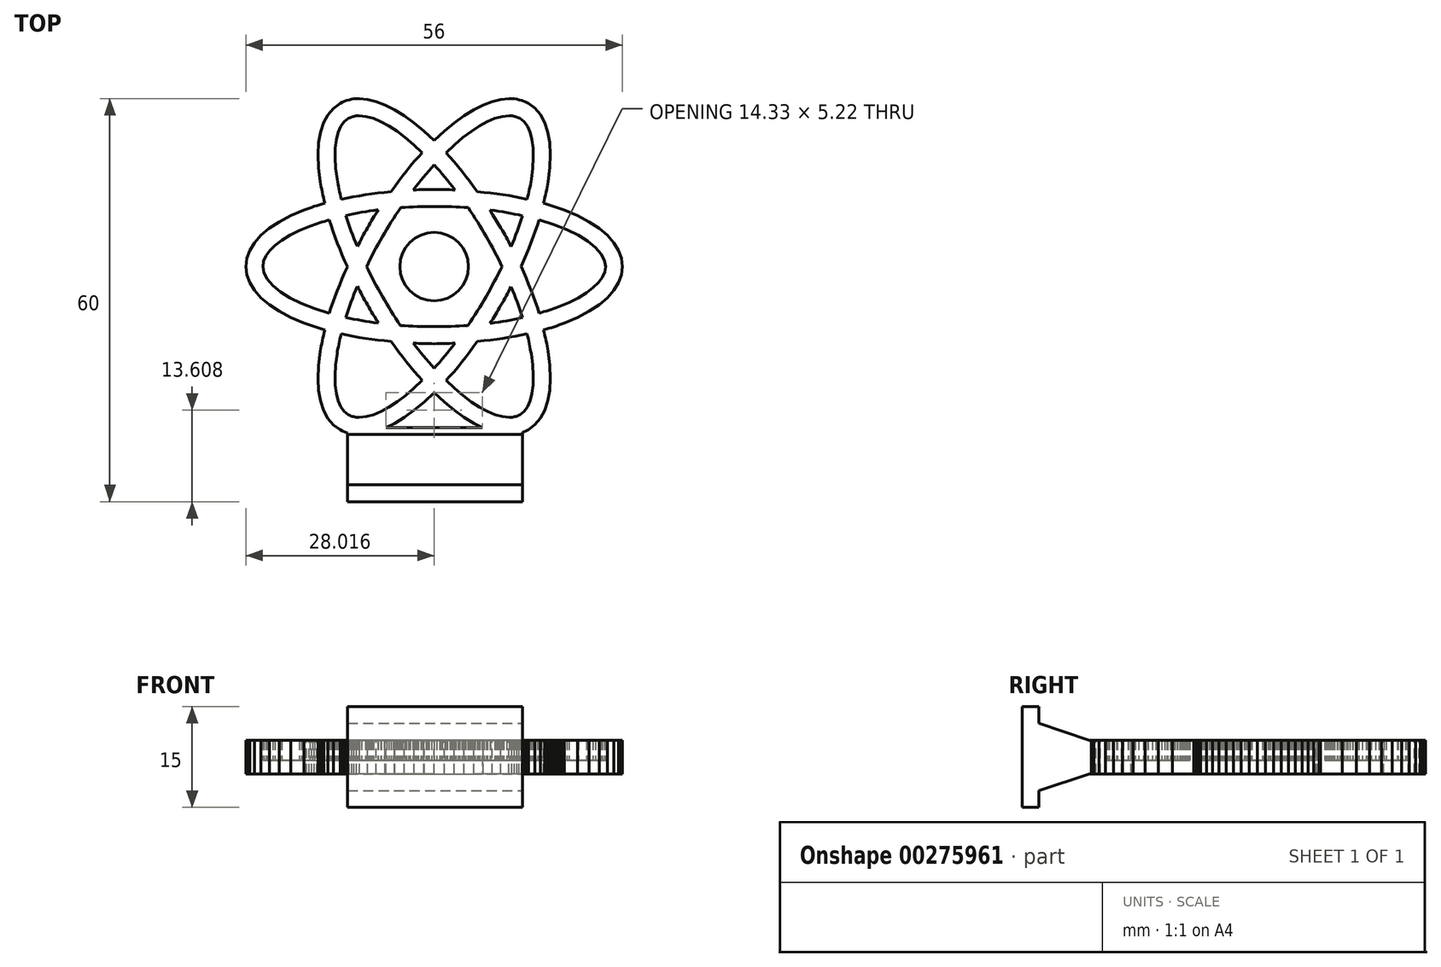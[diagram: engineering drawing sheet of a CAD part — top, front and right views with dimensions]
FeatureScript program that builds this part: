
annotation { "Feature Type Name" : "Feature", "Feature Type Description" : "" }
export const myFeature = defineFeature(function(context is Context, id is Id, definition is map)
    precondition{}
    {
        {
            var Q0;
            Q0=qCreatedBy(makeId("Top.planeOp"),FACE);
            var sketch = newSketch(context, id + "F0", { "sketchPlane" : qUnion([Q0])});
            skLineSegment(sketch, "E0", {"start": v(0, 5.1) * mm, "end": v(1.03, 5) * mm});
            skLineSegment(sketch, "E1", {"start": v(1.03, 5) * mm, "end": v(1.98, 4.7) * mm});
            skLineSegment(sketch, "E2", {"start": v(1.98, 4.7) * mm, "end": v(2.85, 4.23) * mm});
            skLineSegment(sketch, "E3", {"start": v(2.85, 4.23) * mm, "end": v(3.6, 3.6) * mm});
            skLineSegment(sketch, "E4", {"start": v(3.6, 3.6) * mm, "end": v(4.23, 2.85) * mm});
            skLineSegment(sketch, "E5", {"start": v(4.23, 2.85) * mm, "end": v(4.7, 1.98) * mm});
            skLineSegment(sketch, "E6", {"start": v(4.7, 1.98) * mm, "end": v(5, 1.03) * mm});
            skLineSegment(sketch, "E7", {"start": v(5, 1.03) * mm, "end": v(5.1, 0) * mm});
            skLineSegment(sketch, "E8", {"start": v(5.1, 0) * mm, "end": v(5, -1.03) * mm});
            skLineSegment(sketch, "E9", {"start": v(5, -1.03) * mm, "end": v(4.7, -1.98) * mm});
            skLineSegment(sketch, "E10", {"start": v(4.7, -1.98) * mm, "end": v(4.23, -2.85) * mm});
            skLineSegment(sketch, "E11", {"start": v(4.23, -2.85) * mm, "end": v(3.6, -3.6) * mm});
            skLineSegment(sketch, "E12", {"start": v(3.6, -3.6) * mm, "end": v(2.85, -4.23) * mm});
            skLineSegment(sketch, "E13", {"start": v(2.85, -4.23) * mm, "end": v(1.98, -4.7) * mm});
            skLineSegment(sketch, "E14", {"start": v(1.98, -4.7) * mm, "end": v(1.03, -5) * mm});
            skLineSegment(sketch, "E15", {"start": v(1.03, -5) * mm, "end": v(0, -5.1) * mm});
            skLineSegment(sketch, "E16", {"start": v(0, -5.1) * mm, "end": v(-1.03, -5) * mm});
            skLineSegment(sketch, "E17", {"start": v(-1.03, -5) * mm, "end": v(-1.98, -4.7) * mm});
            skLineSegment(sketch, "E18", {"start": v(-1.98, -4.7) * mm, "end": v(-2.85, -4.23) * mm});
            skLineSegment(sketch, "E19", {"start": v(-2.85, -4.23) * mm, "end": v(-3.6, -3.6) * mm});
            skLineSegment(sketch, "E20", {"start": v(-3.6, -3.6) * mm, "end": v(-4.23, -2.85) * mm});
            skLineSegment(sketch, "E21", {"start": v(-4.23, -2.85) * mm, "end": v(-4.7, -1.98) * mm});
            skLineSegment(sketch, "E22", {"start": v(-4.7, -1.98) * mm, "end": v(-5, -1.03) * mm});
            skLineSegment(sketch, "E23", {"start": v(-5, -1.03) * mm, "end": v(-5.1, 0) * mm});
            skLineSegment(sketch, "E24", {"start": v(-5.1, 0) * mm, "end": v(-5, 1.03) * mm});
            skLineSegment(sketch, "E25", {"start": v(-5, 1.03) * mm, "end": v(-4.7, 1.98) * mm});
            skLineSegment(sketch, "E26", {"start": v(-4.7, 1.98) * mm, "end": v(-4.23, 2.85) * mm});
            skLineSegment(sketch, "E27", {"start": v(-4.23, 2.85) * mm, "end": v(-3.6, 3.6) * mm});
            skLineSegment(sketch, "E28", {"start": v(-3.6, 3.6) * mm, "end": v(-2.85, 4.23) * mm});
            skLineSegment(sketch, "E29", {"start": v(-2.85, 4.23) * mm, "end": v(-1.98, 4.7) * mm});
            skLineSegment(sketch, "E30", {"start": v(-1.98, 4.7) * mm, "end": v(-1.03, 5) * mm});
            skLineSegment(sketch, "E31", {"start": v(-1.03, 5) * mm, "end": v(0, 5.1) * mm});
            skLineSegment(sketch, "E32", {"start": v(19.36, 8.4) * mm, "end": v(19, 8.54) * mm});
            skLineSegment(sketch, "E33", {"start": v(19, 8.54) * mm, "end": v(18.62, 8.68) * mm});
            skLineSegment(sketch, "E34", {"start": v(18.62, 8.68) * mm, "end": v(18.24, 8.8) * mm});
            skLineSegment(sketch, "E35", {"start": v(18.24, 8.8) * mm, "end": v(17.86, 8.94) * mm});
            skLineSegment(sketch, "E36", {"start": v(17.86, 8.94) * mm, "end": v(17.47, 9.07) * mm});
            skLineSegment(sketch, "E37", {"start": v(17.47, 9.07) * mm, "end": v(17.08, 9.2) * mm});
            skLineSegment(sketch, "E38", {"start": v(17.08, 9.2) * mm, "end": v(16.68, 9.32) * mm});
            skLineSegment(sketch, "E39", {"start": v(16.68, 9.32) * mm, "end": v(16.28, 9.44) * mm});
            skLineSegment(sketch, "E40", {"start": v(16.28, 9.44) * mm, "end": v(16.38, 9.84) * mm});
            skLineSegment(sketch, "E41", {"start": v(16.38, 9.84) * mm, "end": v(16.47, 10.24) * mm});
            skLineSegment(sketch, "E42", {"start": v(16.47, 10.24) * mm, "end": v(16.56, 10.64) * mm});
            skLineSegment(sketch, "E43", {"start": v(16.56, 10.64) * mm, "end": v(16.65, 11.04) * mm});
            skLineSegment(sketch, "E44", {"start": v(16.65, 11.04) * mm, "end": v(16.73, 11.44) * mm});
            skLineSegment(sketch, "E45", {"start": v(16.73, 11.44) * mm, "end": v(16.8, 11.83) * mm});
            skLineSegment(sketch, "E46", {"start": v(16.8, 11.83) * mm, "end": v(16.88, 12.22) * mm});
            skLineSegment(sketch, "E47", {"start": v(16.88, 12.22) * mm, "end": v(16.95, 12.61) * mm});
            skLineSegment(sketch, "E48", {"start": v(16.95, 12.61) * mm, "end": v(17.21, 14.74) * mm});
            skLineSegment(sketch, "E49", {"start": v(17.21, 14.74) * mm, "end": v(17.29, 16.7) * mm});
            skLineSegment(sketch, "E50", {"start": v(17.29, 16.7) * mm, "end": v(17.18, 18.47) * mm});
            skLineSegment(sketch, "E51", {"start": v(17.18, 18.47) * mm, "end": v(16.9, 20.06) * mm});
            skLineSegment(sketch, "E52", {"start": v(16.9, 20.06) * mm, "end": v(16.44, 21.44) * mm});
            skLineSegment(sketch, "E53", {"start": v(16.44, 21.44) * mm, "end": v(15.8, 22.61) * mm});
            skLineSegment(sketch, "E54", {"start": v(15.8, 22.61) * mm, "end": v(14.99, 23.56) * mm});
            skLineSegment(sketch, "E55", {"start": v(14.99, 23.56) * mm, "end": v(14, 24.28) * mm});
            skLineSegment(sketch, "E56", {"start": v(14, 24.28) * mm, "end": v(13.68, 24.46) * mm});
            skLineSegment(sketch, "E57", {"start": v(13.68, 24.46) * mm, "end": v(13.34, 24.6) * mm});
            skLineSegment(sketch, "E58", {"start": v(13.34, 24.6) * mm, "end": v(13, 24.73) * mm});
            skLineSegment(sketch, "E59", {"start": v(13, 24.73) * mm, "end": v(12.65, 24.83) * mm});
            skLineSegment(sketch, "E60", {"start": v(12.65, 24.83) * mm, "end": v(12.29, 24.9) * mm});
            skLineSegment(sketch, "E61", {"start": v(12.29, 24.9) * mm, "end": v(11.92, 24.96) * mm});
            skLineSegment(sketch, "E62", {"start": v(11.92, 24.96) * mm, "end": v(11.53, 24.99) * mm});
            skLineSegment(sketch, "E63", {"start": v(11.53, 24.99) * mm, "end": v(11.14, 25) * mm});
            skLineSegment(sketch, "E64", {"start": v(11.14, 25) * mm, "end": v(9.92, 24.9) * mm});
            skLineSegment(sketch, "E65", {"start": v(9.92, 24.9) * mm, "end": v(8.64, 24.58) * mm});
            skLineSegment(sketch, "E66", {"start": v(8.64, 24.58) * mm, "end": v(7.3, 24.06) * mm});
            skLineSegment(sketch, "E67", {"start": v(7.3, 24.06) * mm, "end": v(5.9, 23.35) * mm});
            skLineSegment(sketch, "E68", {"start": v(5.9, 23.35) * mm, "end": v(4.47, 22.46) * mm});
            skLineSegment(sketch, "E69", {"start": v(4.47, 22.46) * mm, "end": v(3, 21.4) * mm});
            skLineSegment(sketch, "E70", {"start": v(3, 21.4) * mm, "end": v(1.5, 20.17) * mm});
            skLineSegment(sketch, "E71", {"start": v(1.5, 20.17) * mm, "end": v(0, 18.78) * mm});
            skLineSegment(sketch, "E72", {"start": v(0, 18.78) * mm, "end": v(-1.5, 20.17) * mm});
            skLineSegment(sketch, "E73", {"start": v(-1.5, 20.17) * mm, "end": v(-3, 21.4) * mm});
            skLineSegment(sketch, "E74", {"start": v(-3, 21.4) * mm, "end": v(-4.47, 22.46) * mm});
            skLineSegment(sketch, "E75", {"start": v(-4.47, 22.46) * mm, "end": v(-5.9, 23.35) * mm});
            skLineSegment(sketch, "E76", {"start": v(-5.9, 23.35) * mm, "end": v(-7.3, 24.06) * mm});
            skLineSegment(sketch, "E77", {"start": v(-7.3, 24.06) * mm, "end": v(-8.64, 24.58) * mm});
            skLineSegment(sketch, "E78", {"start": v(-8.64, 24.58) * mm, "end": v(-9.92, 24.9) * mm});
            skLineSegment(sketch, "E79", {"start": v(-9.92, 24.9) * mm, "end": v(-11.14, 25) * mm});
            skLineSegment(sketch, "E80", {"start": v(-11.14, 25) * mm, "end": v(-11.53, 24.99) * mm});
            skLineSegment(sketch, "E81", {"start": v(-11.53, 24.99) * mm, "end": v(-11.92, 24.96) * mm});
            skLineSegment(sketch, "E82", {"start": v(-11.92, 24.96) * mm, "end": v(-12.29, 24.9) * mm});
            skLineSegment(sketch, "E83", {"start": v(-12.29, 24.9) * mm, "end": v(-12.65, 24.83) * mm});
            skLineSegment(sketch, "E84", {"start": v(-12.65, 24.83) * mm, "end": v(-13, 24.73) * mm});
            skLineSegment(sketch, "E85", {"start": v(-13, 24.73) * mm, "end": v(-13.34, 24.6) * mm});
            skLineSegment(sketch, "E86", {"start": v(-13.34, 24.6) * mm, "end": v(-13.68, 24.46) * mm});
            skLineSegment(sketch, "E87", {"start": v(-13.68, 24.46) * mm, "end": v(-14, 24.28) * mm});
            skLineSegment(sketch, "E88", {"start": v(-14, 24.28) * mm, "end": v(-14.99, 23.55) * mm});
            skLineSegment(sketch, "E89", {"start": v(-14.99, 23.55) * mm, "end": v(-15.8, 22.59) * mm});
            skLineSegment(sketch, "E90", {"start": v(-15.8, 22.59) * mm, "end": v(-16.44, 21.4) * mm});
            skLineSegment(sketch, "E91", {"start": v(-16.44, 21.4) * mm, "end": v(-16.9, 20.02) * mm});
            skLineSegment(sketch, "E92", {"start": v(-16.9, 20.02) * mm, "end": v(-17.18, 18.44) * mm});
            skLineSegment(sketch, "E93", {"start": v(-17.18, 18.44) * mm, "end": v(-17.29, 16.67) * mm});
            skLineSegment(sketch, "E94", {"start": v(-17.29, 16.67) * mm, "end": v(-17.21, 14.73) * mm});
            skLineSegment(sketch, "E95", {"start": v(-17.21, 14.73) * mm, "end": v(-16.95, 12.61) * mm});
            skLineSegment(sketch, "E96", {"start": v(-16.95, 12.61) * mm, "end": v(-16.88, 12.22) * mm});
            skLineSegment(sketch, "E97", {"start": v(-16.88, 12.22) * mm, "end": v(-16.8, 11.83) * mm});
            skLineSegment(sketch, "E98", {"start": v(-16.8, 11.83) * mm, "end": v(-16.73, 11.44) * mm});
            skLineSegment(sketch, "E99", {"start": v(-16.73, 11.44) * mm, "end": v(-16.65, 11.04) * mm});
            skLineSegment(sketch, "E100", {"start": v(-16.65, 11.04) * mm, "end": v(-16.56, 10.64) * mm});
            skLineSegment(sketch, "E101", {"start": v(-16.56, 10.64) * mm, "end": v(-16.47, 10.24) * mm});
            skLineSegment(sketch, "E102", {"start": v(-16.47, 10.24) * mm, "end": v(-16.38, 9.84) * mm});
            skLineSegment(sketch, "E103", {"start": v(-16.38, 9.84) * mm, "end": v(-16.28, 9.44) * mm});
            skLineSegment(sketch, "E104", {"start": v(-16.28, 9.44) * mm, "end": v(-16.68, 9.32) * mm});
            skLineSegment(sketch, "E105", {"start": v(-16.68, 9.32) * mm, "end": v(-17.08, 9.2) * mm});
            skLineSegment(sketch, "E106", {"start": v(-17.08, 9.2) * mm, "end": v(-17.47, 9.08) * mm});
            skLineSegment(sketch, "E107", {"start": v(-17.47, 9.08) * mm, "end": v(-17.86, 8.96) * mm});
            skLineSegment(sketch, "E108", {"start": v(-17.86, 8.96) * mm, "end": v(-18.24, 8.83) * mm});
            skLineSegment(sketch, "E109", {"start": v(-18.24, 8.83) * mm, "end": v(-18.62, 8.7) * mm});
            skLineSegment(sketch, "E110", {"start": v(-18.62, 8.7) * mm, "end": v(-19, 8.55) * mm});
            skLineSegment(sketch, "E111", {"start": v(-19, 8.55) * mm, "end": v(-19.36, 8.4) * mm});
            skLineSegment(sketch, "E112", {"start": v(-19.36, 8.4) * mm, "end": v(-21.34, 7.57) * mm});
            skLineSegment(sketch, "E113", {"start": v(-21.34, 7.57) * mm, "end": v(-23.07, 6.65) * mm});
            skLineSegment(sketch, "E114", {"start": v(-23.07, 6.65) * mm, "end": v(-24.55, 5.68) * mm});
            skLineSegment(sketch, "E115", {"start": v(-24.55, 5.68) * mm, "end": v(-25.78, 4.64) * mm});
            skLineSegment(sketch, "E116", {"start": v(-25.78, 4.64) * mm, "end": v(-26.74, 3.55) * mm});
            skLineSegment(sketch, "E117", {"start": v(-26.74, 3.55) * mm, "end": v(-27.43, 2.4) * mm});
            skLineSegment(sketch, "E118", {"start": v(-27.43, 2.4) * mm, "end": v(-27.85, 1.22) * mm});
            skLineSegment(sketch, "E119", {"start": v(-27.85, 1.22) * mm, "end": v(-28, 0) * mm});
            skLineSegment(sketch, "E120", {"start": v(-28, 0) * mm, "end": v(-27.85, -1.22) * mm});
            skLineSegment(sketch, "E121", {"start": v(-27.85, -1.22) * mm, "end": v(-27.43, -2.4) * mm});
            skLineSegment(sketch, "E122", {"start": v(-27.43, -2.4) * mm, "end": v(-26.73, -3.55) * mm});
            skLineSegment(sketch, "E123", {"start": v(-26.73, -3.55) * mm, "end": v(-25.76, -4.64) * mm});
            skLineSegment(sketch, "E124", {"start": v(-25.76, -4.64) * mm, "end": v(-24.53, -5.68) * mm});
            skLineSegment(sketch, "E125", {"start": v(-24.53, -5.68) * mm, "end": v(-23.05, -6.65) * mm});
            skLineSegment(sketch, "E126", {"start": v(-23.05, -6.65) * mm, "end": v(-21.33, -7.57) * mm});
            skLineSegment(sketch, "E127", {"start": v(-21.33, -7.57) * mm, "end": v(-19.36, -8.4) * mm});
            skLineSegment(sketch, "E128", {"start": v(-19.36, -8.4) * mm, "end": v(-19, -8.54) * mm});
            skLineSegment(sketch, "E129", {"start": v(-19, -8.54) * mm, "end": v(-18.62, -8.68) * mm});
            skLineSegment(sketch, "E130", {"start": v(-18.62, -8.68) * mm, "end": v(-18.24, -8.8) * mm});
            skLineSegment(sketch, "E131", {"start": v(-18.24, -8.8) * mm, "end": v(-17.86, -8.94) * mm});
            skLineSegment(sketch, "E132", {"start": v(-17.86, -8.94) * mm, "end": v(-17.47, -9.07) * mm});
            skLineSegment(sketch, "E133", {"start": v(-17.47, -9.07) * mm, "end": v(-17.08, -9.2) * mm});
            skLineSegment(sketch, "E134", {"start": v(-17.08, -9.2) * mm, "end": v(-16.68, -9.32) * mm});
            skLineSegment(sketch, "E135", {"start": v(-16.68, -9.32) * mm, "end": v(-16.28, -9.44) * mm});
            skLineSegment(sketch, "E136", {"start": v(-16.28, -9.44) * mm, "end": v(-16.38, -9.84) * mm});
            skLineSegment(sketch, "E137", {"start": v(-16.38, -9.84) * mm, "end": v(-16.47, -10.24) * mm});
            skLineSegment(sketch, "E138", {"start": v(-16.47, -10.24) * mm, "end": v(-16.56, -10.64) * mm});
            skLineSegment(sketch, "E139", {"start": v(-16.56, -10.64) * mm, "end": v(-16.65, -11.04) * mm});
            skLineSegment(sketch, "E140", {"start": v(-16.65, -11.04) * mm, "end": v(-16.73, -11.44) * mm});
            skLineSegment(sketch, "E141", {"start": v(-16.73, -11.44) * mm, "end": v(-16.8, -11.83) * mm});
            skLineSegment(sketch, "E142", {"start": v(-16.8, -11.83) * mm, "end": v(-16.88, -12.22) * mm});
            skLineSegment(sketch, "E143", {"start": v(-16.88, -12.22) * mm, "end": v(-16.95, -12.61) * mm});
            skLineSegment(sketch, "E144", {"start": v(-16.95, -12.61) * mm, "end": v(-17.21, -14.74) * mm});
            skLineSegment(sketch, "E145", {"start": v(-17.21, -14.74) * mm, "end": v(-17.29, -16.7) * mm});
            skLineSegment(sketch, "E146", {"start": v(-17.29, -16.7) * mm, "end": v(-17.18, -18.47) * mm});
            skLineSegment(sketch, "E147", {"start": v(-17.18, -18.47) * mm, "end": v(-16.9, -20.06) * mm});
            skLineSegment(sketch, "E148", {"start": v(-16.9, -20.06) * mm, "end": v(-16.44, -21.44) * mm});
            skLineSegment(sketch, "E149", {"start": v(-16.44, -21.44) * mm, "end": v(-15.8, -22.61) * mm});
            skLineSegment(sketch, "E150", {"start": v(-15.8, -22.61) * mm, "end": v(-14.99, -23.56) * mm});
            skLineSegment(sketch, "E151", {"start": v(-14.99, -23.56) * mm, "end": v(-14, -24.28) * mm});
            skLineSegment(sketch, "E152", {"start": v(-14, -24.28) * mm, "end": v(-13.68, -24.46) * mm});
            skLineSegment(sketch, "E153", {"start": v(-13.68, -24.46) * mm, "end": v(-13.34, -24.6) * mm});
            skLineSegment(sketch, "E154", {"start": v(-13.34, -24.6) * mm, "end": v(-13, -24.73) * mm});
            skLineSegment(sketch, "E155", {"start": v(-13, -24.73) * mm, "end": v(-12.65, -24.83) * mm});
            skLineSegment(sketch, "E156", {"start": v(-12.65, -24.83) * mm, "end": v(-12.29, -24.9) * mm});
            skLineSegment(sketch, "E157", {"start": v(-12.29, -24.9) * mm, "end": v(-11.92, -24.96) * mm});
            skLineSegment(sketch, "E158", {"start": v(-11.92, -24.96) * mm, "end": v(-11.53, -24.99) * mm});
            skLineSegment(sketch, "E159", {"start": v(-11.53, -24.99) * mm, "end": v(-11.14, -25) * mm});
            skLineSegment(sketch, "E160", {"start": v(-11.14, -25) * mm, "end": v(-9.9, -24.9) * mm});
            skLineSegment(sketch, "E161", {"start": v(-9.9, -24.9) * mm, "end": v(-8.62, -24.58) * mm});
            skLineSegment(sketch, "E162", {"start": v(-8.62, -24.58) * mm, "end": v(-7.27, -24.06) * mm});
            skLineSegment(sketch, "E163", {"start": v(-7.27, -24.06) * mm, "end": v(-5.87, -23.35) * mm});
            skLineSegment(sketch, "E164", {"start": v(-5.87, -23.35) * mm, "end": v(-4.44, -22.46) * mm});
            skLineSegment(sketch, "E165", {"start": v(-4.44, -22.46) * mm, "end": v(-2.97, -21.4) * mm});
            skLineSegment(sketch, "E166", {"start": v(-2.97, -21.4) * mm, "end": v(-1.5, -20.17) * mm});
            skLineSegment(sketch, "E167", {"start": v(-1.5, -20.17) * mm, "end": v(0, -18.78) * mm});
            skLineSegment(sketch, "E168", {"start": v(0, -18.78) * mm, "end": v(1.5, -20.17) * mm});
            skLineSegment(sketch, "E169", {"start": v(1.5, -20.17) * mm, "end": v(3, -21.4) * mm});
            skLineSegment(sketch, "E170", {"start": v(3, -21.4) * mm, "end": v(4.47, -22.46) * mm});
            skLineSegment(sketch, "E171", {"start": v(4.47, -22.46) * mm, "end": v(5.9, -23.35) * mm});
            skLineSegment(sketch, "E172", {"start": v(5.9, -23.35) * mm, "end": v(7.3, -24.06) * mm});
            skLineSegment(sketch, "E173", {"start": v(7.3, -24.06) * mm, "end": v(8.64, -24.58) * mm});
            skLineSegment(sketch, "E174", {"start": v(8.64, -24.58) * mm, "end": v(9.92, -24.9) * mm});
            skLineSegment(sketch, "E175", {"start": v(9.92, -24.9) * mm, "end": v(11.14, -25) * mm});
            skLineSegment(sketch, "E176", {"start": v(11.14, -25) * mm, "end": v(11.53, -24.99) * mm});
            skLineSegment(sketch, "E177", {"start": v(11.53, -24.99) * mm, "end": v(11.92, -24.96) * mm});
            skLineSegment(sketch, "E178", {"start": v(11.92, -24.96) * mm, "end": v(12.29, -24.9) * mm});
            skLineSegment(sketch, "E179", {"start": v(12.29, -24.9) * mm, "end": v(12.65, -24.83) * mm});
            skLineSegment(sketch, "E180", {"start": v(12.65, -24.83) * mm, "end": v(13, -24.73) * mm});
            skLineSegment(sketch, "E181", {"start": v(13, -24.73) * mm, "end": v(13.34, -24.6) * mm});
            skLineSegment(sketch, "E182", {"start": v(13.34, -24.6) * mm, "end": v(13.68, -24.46) * mm});
            skLineSegment(sketch, "E183", {"start": v(13.68, -24.46) * mm, "end": v(14, -24.28) * mm});
            skLineSegment(sketch, "E184", {"start": v(14, -24.28) * mm, "end": v(14.99, -23.55) * mm});
            skLineSegment(sketch, "E185", {"start": v(14.99, -23.55) * mm, "end": v(15.8, -22.59) * mm});
            skLineSegment(sketch, "E186", {"start": v(15.8, -22.59) * mm, "end": v(16.44, -21.4) * mm});
            skLineSegment(sketch, "E187", {"start": v(16.44, -21.4) * mm, "end": v(16.9, -20.02) * mm});
            skLineSegment(sketch, "E188", {"start": v(16.9, -20.02) * mm, "end": v(17.18, -18.44) * mm});
            skLineSegment(sketch, "E189", {"start": v(17.18, -18.44) * mm, "end": v(17.29, -16.67) * mm});
            skLineSegment(sketch, "E190", {"start": v(17.29, -16.67) * mm, "end": v(17.21, -14.73) * mm});
            skLineSegment(sketch, "E191", {"start": v(17.21, -14.73) * mm, "end": v(16.95, -12.61) * mm});
            skLineSegment(sketch, "E192", {"start": v(16.95, -12.61) * mm, "end": v(16.88, -12.22) * mm});
            skLineSegment(sketch, "E193", {"start": v(16.88, -12.22) * mm, "end": v(16.8, -11.83) * mm});
            skLineSegment(sketch, "E194", {"start": v(16.8, -11.83) * mm, "end": v(16.73, -11.44) * mm});
            skLineSegment(sketch, "E195", {"start": v(16.73, -11.44) * mm, "end": v(16.65, -11.04) * mm});
            skLineSegment(sketch, "E196", {"start": v(16.65, -11.04) * mm, "end": v(16.56, -10.64) * mm});
            skLineSegment(sketch, "E197", {"start": v(16.56, -10.64) * mm, "end": v(16.47, -10.24) * mm});
            skLineSegment(sketch, "E198", {"start": v(16.47, -10.24) * mm, "end": v(16.38, -9.84) * mm});
            skLineSegment(sketch, "E199", {"start": v(16.38, -9.84) * mm, "end": v(16.28, -9.44) * mm});
            skLineSegment(sketch, "E200", {"start": v(16.28, -9.44) * mm, "end": v(16.68, -9.32) * mm});
            skLineSegment(sketch, "E201", {"start": v(16.68, -9.32) * mm, "end": v(17.08, -9.2) * mm});
            skLineSegment(sketch, "E202", {"start": v(17.08, -9.2) * mm, "end": v(17.47, -9.08) * mm});
            skLineSegment(sketch, "E203", {"start": v(17.47, -9.08) * mm, "end": v(17.86, -8.96) * mm});
            skLineSegment(sketch, "E204", {"start": v(17.86, -8.96) * mm, "end": v(18.24, -8.83) * mm});
            skLineSegment(sketch, "E205", {"start": v(18.24, -8.83) * mm, "end": v(18.62, -8.7) * mm});
            skLineSegment(sketch, "E206", {"start": v(18.62, -8.7) * mm, "end": v(19, -8.55) * mm});
            skLineSegment(sketch, "E207", {"start": v(19, -8.55) * mm, "end": v(19.36, -8.4) * mm});
            skLineSegment(sketch, "E208", {"start": v(19.36, -8.4) * mm, "end": v(21.34, -7.57) * mm});
            skLineSegment(sketch, "E209", {"start": v(21.34, -7.57) * mm, "end": v(23.07, -6.65) * mm});
            skLineSegment(sketch, "E210", {"start": v(23.07, -6.65) * mm, "end": v(24.55, -5.68) * mm});
            skLineSegment(sketch, "E211", {"start": v(24.55, -5.68) * mm, "end": v(25.78, -4.64) * mm});
            skLineSegment(sketch, "E212", {"start": v(25.78, -4.64) * mm, "end": v(26.74, -3.55) * mm});
            skLineSegment(sketch, "E213", {"start": v(26.74, -3.55) * mm, "end": v(27.43, -2.4) * mm});
            skLineSegment(sketch, "E214", {"start": v(27.43, -2.4) * mm, "end": v(27.85, -1.22) * mm});
            skLineSegment(sketch, "E215", {"start": v(27.85, -1.22) * mm, "end": v(28, 0) * mm});
            skLineSegment(sketch, "E216", {"start": v(28, 0) * mm, "end": v(27.85, 1.22) * mm});
            skLineSegment(sketch, "E217", {"start": v(27.85, 1.22) * mm, "end": v(27.43, 2.4) * mm});
            skLineSegment(sketch, "E218", {"start": v(27.43, 2.4) * mm, "end": v(26.74, 3.55) * mm});
            skLineSegment(sketch, "E219", {"start": v(26.74, 3.55) * mm, "end": v(25.78, 4.64) * mm});
            skLineSegment(sketch, "E220", {"start": v(25.78, 4.64) * mm, "end": v(24.55, 5.68) * mm});
            skLineSegment(sketch, "E221", {"start": v(24.55, 5.68) * mm, "end": v(23.07, 6.65) * mm});
            skLineSegment(sketch, "E222", {"start": v(23.07, 6.65) * mm, "end": v(21.34, 7.57) * mm});
            skLineSegment(sketch, "E223", {"start": v(21.34, 7.57) * mm, "end": v(19.36, 8.4) * mm});
            skLineSegment(sketch, "E224", {"start": v(12.75, 22.05) * mm, "end": v(13.38, 21.54) * mm});
            skLineSegment(sketch, "E225", {"start": v(13.38, 21.54) * mm, "end": v(13.9, 20.84) * mm});
            skLineSegment(sketch, "E226", {"start": v(13.9, 20.84) * mm, "end": v(14.29, 19.94) * mm});
            skLineSegment(sketch, "E227", {"start": v(14.29, 19.94) * mm, "end": v(14.57, 18.87) * mm});
            skLineSegment(sketch, "E228", {"start": v(14.57, 18.87) * mm, "end": v(14.73, 17.62) * mm});
            skLineSegment(sketch, "E229", {"start": v(14.73, 17.62) * mm, "end": v(14.76, 16.22) * mm});
            skLineSegment(sketch, "E230", {"start": v(14.76, 16.22) * mm, "end": v(14.67, 14.66) * mm});
            skLineSegment(sketch, "E231", {"start": v(14.67, 14.66) * mm, "end": v(14.45, 12.97) * mm});
            skLineSegment(sketch, "E232", {"start": v(14.45, 12.97) * mm, "end": v(14.4, 12.62) * mm});
            skLineSegment(sketch, "E233", {"start": v(14.4, 12.62) * mm, "end": v(14.33, 12.26) * mm});
            skLineSegment(sketch, "E234", {"start": v(14.33, 12.26) * mm, "end": v(14.26, 11.9) * mm});
            skLineSegment(sketch, "E235", {"start": v(14.26, 11.9) * mm, "end": v(14.18, 11.53) * mm});
            skLineSegment(sketch, "E236", {"start": v(14.18, 11.53) * mm, "end": v(14.1, 11.16) * mm});
            skLineSegment(sketch, "E237", {"start": v(14.1, 11.16) * mm, "end": v(14.01, 10.78) * mm});
            skLineSegment(sketch, "E238", {"start": v(14.01, 10.78) * mm, "end": v(13.92, 10.4) * mm});
            skLineSegment(sketch, "E239", {"start": v(13.92, 10.4) * mm, "end": v(13.82, 10.02) * mm});
            skLineSegment(sketch, "E240", {"start": v(13.82, 10.02) * mm, "end": v(12.94, 10.21) * mm});
            skLineSegment(sketch, "E241", {"start": v(12.94, 10.21) * mm, "end": v(12.05, 10.39) * mm});
            skLineSegment(sketch, "E242", {"start": v(12.05, 10.39) * mm, "end": v(11.15, 10.55) * mm});
            skLineSegment(sketch, "E243", {"start": v(11.15, 10.55) * mm, "end": v(10.23, 10.7) * mm});
            skLineSegment(sketch, "E244", {"start": v(10.23, 10.7) * mm, "end": v(9.3, 10.83) * mm});
            skLineSegment(sketch, "E245", {"start": v(9.3, 10.83) * mm, "end": v(8.36, 10.94) * mm});
            skLineSegment(sketch, "E246", {"start": v(8.36, 10.94) * mm, "end": v(7.4, 11.05) * mm});
            skLineSegment(sketch, "E247", {"start": v(7.4, 11.05) * mm, "end": v(6.44, 11.14) * mm});
            skLineSegment(sketch, "E248", {"start": v(6.44, 11.14) * mm, "end": v(5.87, 11.93) * mm});
            skLineSegment(sketch, "E249", {"start": v(5.87, 11.93) * mm, "end": v(5.3, 12.7) * mm});
            skLineSegment(sketch, "E250", {"start": v(5.3, 12.7) * mm, "end": v(4.71, 13.46) * mm});
            skLineSegment(sketch, "E251", {"start": v(4.71, 13.46) * mm, "end": v(4.13, 14.2) * mm});
            skLineSegment(sketch, "E252", {"start": v(4.13, 14.2) * mm, "end": v(3.55, 14.9) * mm});
            skLineSegment(sketch, "E253", {"start": v(3.55, 14.9) * mm, "end": v(2.96, 15.6) * mm});
            skLineSegment(sketch, "E254", {"start": v(2.96, 15.6) * mm, "end": v(2.38, 16.29) * mm});
            skLineSegment(sketch, "E255", {"start": v(2.38, 16.29) * mm, "end": v(1.79, 16.95) * mm});
            skLineSegment(sketch, "E256", {"start": v(1.79, 16.95) * mm, "end": v(3.03, 18.12) * mm});
            skLineSegment(sketch, "E257", {"start": v(3.03, 18.12) * mm, "end": v(4.27, 19.19) * mm});
            skLineSegment(sketch, "E258", {"start": v(4.27, 19.19) * mm, "end": v(5.5, 20.13) * mm});
            skLineSegment(sketch, "E259", {"start": v(5.5, 20.13) * mm, "end": v(6.7, 20.92) * mm});
            skLineSegment(sketch, "E260", {"start": v(6.7, 20.92) * mm, "end": v(7.88, 21.57) * mm});
            skLineSegment(sketch, "E261", {"start": v(7.88, 21.57) * mm, "end": v(9.03, 22.05) * mm});
            skLineSegment(sketch, "E262", {"start": v(9.03, 22.05) * mm, "end": v(10.13, 22.35) * mm});
            skLineSegment(sketch, "E263", {"start": v(10.13, 22.35) * mm, "end": v(11.18, 22.45) * mm});
            skLineSegment(sketch, "E264", {"start": v(11.18, 22.45) * mm, "end": v(11.4, 22.44) * mm});
            skLineSegment(sketch, "E265", {"start": v(11.4, 22.44) * mm, "end": v(11.6, 22.43) * mm});
            skLineSegment(sketch, "E266", {"start": v(11.6, 22.43) * mm, "end": v(11.81, 22.4) * mm});
            skLineSegment(sketch, "E267", {"start": v(11.81, 22.4) * mm, "end": v(12.01, 22.35) * mm});
            skLineSegment(sketch, "E268", {"start": v(12.01, 22.35) * mm, "end": v(12.2, 22.3) * mm});
            skLineSegment(sketch, "E269", {"start": v(12.2, 22.3) * mm, "end": v(12.4, 22.22) * mm});
            skLineSegment(sketch, "E270", {"start": v(12.4, 22.22) * mm, "end": v(12.57, 22.14) * mm});
            skLineSegment(sketch, "E271", {"start": v(12.57, 22.14) * mm, "end": v(12.75, 22.05) * mm});
            skLineSegment(sketch, "E272", {"start": v(7.74, -4.47) * mm, "end": v(7.43, -5) * mm});
            skLineSegment(sketch, "E273", {"start": v(7.43, -5) * mm, "end": v(7.1, -5.55) * mm});
            skLineSegment(sketch, "E274", {"start": v(7.1, -5.55) * mm, "end": v(6.78, -6.08) * mm});
            skLineSegment(sketch, "E275", {"start": v(6.78, -6.08) * mm, "end": v(6.44, -6.62) * mm});
            skLineSegment(sketch, "E276", {"start": v(6.44, -6.62) * mm, "end": v(6.1, -7.16) * mm});
            skLineSegment(sketch, "E277", {"start": v(6.1, -7.16) * mm, "end": v(5.74, -7.7) * mm});
            skLineSegment(sketch, "E278", {"start": v(5.74, -7.7) * mm, "end": v(5.38, -8.23) * mm});
            skLineSegment(sketch, "E279", {"start": v(5.38, -8.23) * mm, "end": v(5, -8.77) * mm});
            skLineSegment(sketch, "E280", {"start": v(5, -8.77) * mm, "end": v(4.39, -8.81) * mm});
            skLineSegment(sketch, "E281", {"start": v(4.39, -8.81) * mm, "end": v(3.77, -8.85) * mm});
            skLineSegment(sketch, "E282", {"start": v(3.77, -8.85) * mm, "end": v(3.15, -8.88) * mm});
            skLineSegment(sketch, "E283", {"start": v(3.15, -8.88) * mm, "end": v(2.52, -8.9) * mm});
            skLineSegment(sketch, "E284", {"start": v(2.52, -8.9) * mm, "end": v(1.9, -8.92) * mm});
            skLineSegment(sketch, "E285", {"start": v(1.9, -8.92) * mm, "end": v(1.27, -8.94) * mm});
            skLineSegment(sketch, "E286", {"start": v(1.27, -8.94) * mm, "end": v(0.64, -8.94) * mm});
            skLineSegment(sketch, "E287", {"start": v(0.64, -8.94) * mm, "end": v(0, -8.94) * mm});
            skLineSegment(sketch, "E288", {"start": v(0, -8.94) * mm, "end": v(-0.65, -8.94) * mm});
            skLineSegment(sketch, "E289", {"start": v(-0.65, -8.94) * mm, "end": v(-1.3, -8.94) * mm});
            skLineSegment(sketch, "E290", {"start": v(-1.3, -8.94) * mm, "end": v(-1.93, -8.92) * mm});
            skLineSegment(sketch, "E291", {"start": v(-1.93, -8.92) * mm, "end": v(-2.55, -8.9) * mm});
            skLineSegment(sketch, "E292", {"start": v(-2.55, -8.9) * mm, "end": v(-3.18, -8.88) * mm});
            skLineSegment(sketch, "E293", {"start": v(-3.18, -8.88) * mm, "end": v(-3.8, -8.85) * mm});
            skLineSegment(sketch, "E294", {"start": v(-3.8, -8.85) * mm, "end": v(-4.4, -8.81) * mm});
            skLineSegment(sketch, "E295", {"start": v(-4.4, -8.81) * mm, "end": v(-5, -8.77) * mm});
            skLineSegment(sketch, "E296", {"start": v(-5, -8.77) * mm, "end": v(-5.37, -8.23) * mm});
            skLineSegment(sketch, "E297", {"start": v(-5.37, -8.23) * mm, "end": v(-5.73, -7.7) * mm});
            skLineSegment(sketch, "E298", {"start": v(-5.73, -7.7) * mm, "end": v(-6.08, -7.16) * mm});
            skLineSegment(sketch, "E299", {"start": v(-6.08, -7.16) * mm, "end": v(-6.42, -6.62) * mm});
            skLineSegment(sketch, "E300", {"start": v(-6.42, -6.62) * mm, "end": v(-6.75, -6.08) * mm});
            skLineSegment(sketch, "E301", {"start": v(-6.75, -6.08) * mm, "end": v(-7.07, -5.55) * mm});
            skLineSegment(sketch, "E302", {"start": v(-7.07, -5.55) * mm, "end": v(-7.39, -5) * mm});
            skLineSegment(sketch, "E303", {"start": v(-7.39, -5) * mm, "end": v(-7.7, -4.47) * mm});
            skLineSegment(sketch, "E304", {"start": v(-7.7, -4.47) * mm, "end": v(-8, -3.92) * mm});
            skLineSegment(sketch, "E305", {"start": v(-8, -3.92) * mm, "end": v(-8.32, -3.36) * mm});
            skLineSegment(sketch, "E306", {"start": v(-8.32, -3.36) * mm, "end": v(-8.63, -2.8) * mm});
            skLineSegment(sketch, "E307", {"start": v(-8.63, -2.8) * mm, "end": v(-8.93, -2.24) * mm});
            skLineSegment(sketch, "E308", {"start": v(-8.93, -2.24) * mm, "end": v(-9.22, -1.67) * mm});
            skLineSegment(sketch, "E309", {"start": v(-9.22, -1.67) * mm, "end": v(-9.5, -1.11) * mm});
            skLineSegment(sketch, "E310", {"start": v(-9.5, -1.11) * mm, "end": v(-9.8, -0.56) * mm});
            skLineSegment(sketch, "E311", {"start": v(-9.8, -0.56) * mm, "end": v(-10.06, 0) * mm});
            skLineSegment(sketch, "E312", {"start": v(-10.06, 0) * mm, "end": v(-9.8, 0.56) * mm});
            skLineSegment(sketch, "E313", {"start": v(-9.8, 0.56) * mm, "end": v(-9.5, 1.11) * mm});
            skLineSegment(sketch, "E314", {"start": v(-9.5, 1.11) * mm, "end": v(-9.22, 1.67) * mm});
            skLineSegment(sketch, "E315", {"start": v(-9.22, 1.67) * mm, "end": v(-8.93, 2.24) * mm});
            skLineSegment(sketch, "E316", {"start": v(-8.93, 2.24) * mm, "end": v(-8.63, 2.8) * mm});
            skLineSegment(sketch, "E317", {"start": v(-8.63, 2.8) * mm, "end": v(-8.32, 3.36) * mm});
            skLineSegment(sketch, "E318", {"start": v(-8.32, 3.36) * mm, "end": v(-8, 3.92) * mm});
            skLineSegment(sketch, "E319", {"start": v(-8, 3.92) * mm, "end": v(-7.7, 4.47) * mm});
            skLineSegment(sketch, "E320", {"start": v(-7.7, 4.47) * mm, "end": v(-7.38, 5) * mm});
            skLineSegment(sketch, "E321", {"start": v(-7.38, 5) * mm, "end": v(-7.06, 5.55) * mm});
            skLineSegment(sketch, "E322", {"start": v(-7.06, 5.55) * mm, "end": v(-6.73, 6.08) * mm});
            skLineSegment(sketch, "E323", {"start": v(-6.73, 6.08) * mm, "end": v(-6.4, 6.62) * mm});
            skLineSegment(sketch, "E324", {"start": v(-6.4, 6.62) * mm, "end": v(-6.05, 7.16) * mm});
            skLineSegment(sketch, "E325", {"start": v(-6.05, 7.16) * mm, "end": v(-5.7, 7.7) * mm});
            skLineSegment(sketch, "E326", {"start": v(-5.7, 7.7) * mm, "end": v(-5.33, 8.23) * mm});
            skLineSegment(sketch, "E327", {"start": v(-5.33, 8.23) * mm, "end": v(-4.96, 8.77) * mm});
            skLineSegment(sketch, "E328", {"start": v(-4.96, 8.77) * mm, "end": v(-4.34, 8.81) * mm});
            skLineSegment(sketch, "E329", {"start": v(-4.34, 8.81) * mm, "end": v(-3.72, 8.85) * mm});
            skLineSegment(sketch, "E330", {"start": v(-3.72, 8.85) * mm, "end": v(-3.1, 8.88) * mm});
            skLineSegment(sketch, "E331", {"start": v(-3.1, 8.88) * mm, "end": v(-2.48, 8.9) * mm});
            skLineSegment(sketch, "E332", {"start": v(-2.48, 8.9) * mm, "end": v(-1.85, 8.92) * mm});
            skLineSegment(sketch, "E333", {"start": v(-1.85, 8.92) * mm, "end": v(-1.22, 8.94) * mm});
            skLineSegment(sketch, "E334", {"start": v(-1.22, 8.94) * mm, "end": v(-0.6, 8.94) * mm});
            skLineSegment(sketch, "E335", {"start": v(-0.6, 8.94) * mm, "end": v(0.04, 8.94) * mm});
            skLineSegment(sketch, "E336", {"start": v(0.04, 8.94) * mm, "end": v(0.7, 8.94) * mm});
            skLineSegment(sketch, "E337", {"start": v(0.7, 8.94) * mm, "end": v(1.34, 8.94) * mm});
            skLineSegment(sketch, "E338", {"start": v(1.34, 8.94) * mm, "end": v(1.97, 8.92) * mm});
            skLineSegment(sketch, "E339", {"start": v(1.97, 8.92) * mm, "end": v(2.6, 8.9) * mm});
            skLineSegment(sketch, "E340", {"start": v(2.6, 8.9) * mm, "end": v(3.22, 8.88) * mm});
            skLineSegment(sketch, "E341", {"start": v(3.22, 8.88) * mm, "end": v(3.84, 8.85) * mm});
            skLineSegment(sketch, "E342", {"start": v(3.84, 8.85) * mm, "end": v(4.45, 8.81) * mm});
            skLineSegment(sketch, "E343", {"start": v(4.45, 8.81) * mm, "end": v(5.05, 8.77) * mm});
            skLineSegment(sketch, "E344", {"start": v(5.05, 8.77) * mm, "end": v(5.42, 8.23) * mm});
            skLineSegment(sketch, "E345", {"start": v(5.42, 8.23) * mm, "end": v(5.77, 7.7) * mm});
            skLineSegment(sketch, "E346", {"start": v(5.77, 7.7) * mm, "end": v(6.12, 7.16) * mm});
            skLineSegment(sketch, "E347", {"start": v(6.12, 7.16) * mm, "end": v(6.46, 6.62) * mm});
            skLineSegment(sketch, "E348", {"start": v(6.46, 6.62) * mm, "end": v(6.8, 6.08) * mm});
            skLineSegment(sketch, "E349", {"start": v(6.8, 6.08) * mm, "end": v(7.12, 5.55) * mm});
            skLineSegment(sketch, "E350", {"start": v(7.12, 5.55) * mm, "end": v(7.43, 5) * mm});
            skLineSegment(sketch, "E351", {"start": v(7.43, 5) * mm, "end": v(7.74, 4.47) * mm});
            skLineSegment(sketch, "E352", {"start": v(7.74, 4.47) * mm, "end": v(8.05, 3.92) * mm});
            skLineSegment(sketch, "E353", {"start": v(8.05, 3.92) * mm, "end": v(8.37, 3.36) * mm});
            skLineSegment(sketch, "E354", {"start": v(8.37, 3.36) * mm, "end": v(8.67, 2.8) * mm});
            skLineSegment(sketch, "E355", {"start": v(8.67, 2.8) * mm, "end": v(8.97, 2.24) * mm});
            skLineSegment(sketch, "E356", {"start": v(8.97, 2.24) * mm, "end": v(9.27, 1.67) * mm});
            skLineSegment(sketch, "E357", {"start": v(9.27, 1.67) * mm, "end": v(9.55, 1.11) * mm});
            skLineSegment(sketch, "E358", {"start": v(9.55, 1.11) * mm, "end": v(9.83, 0.56) * mm});
            skLineSegment(sketch, "E359", {"start": v(9.83, 0.56) * mm, "end": v(10.1, 0) * mm});
            skLineSegment(sketch, "E360", {"start": v(10.1, 0) * mm, "end": v(9.82, -0.55) * mm});
            skLineSegment(sketch, "E361", {"start": v(9.82, -0.55) * mm, "end": v(9.54, -1.1) * mm});
            skLineSegment(sketch, "E362", {"start": v(9.54, -1.1) * mm, "end": v(9.25, -1.66) * mm});
            skLineSegment(sketch, "E363", {"start": v(9.25, -1.66) * mm, "end": v(8.96, -2.22) * mm});
            skLineSegment(sketch, "E364", {"start": v(8.96, -2.22) * mm, "end": v(8.66, -2.78) * mm});
            skLineSegment(sketch, "E365", {"start": v(8.66, -2.78) * mm, "end": v(8.36, -3.34) * mm});
            skLineSegment(sketch, "E366", {"start": v(8.36, -3.34) * mm, "end": v(8.05, -3.9) * mm});
            skLineSegment(sketch, "E367", {"start": v(8.05, -3.9) * mm, "end": v(7.74, -4.47) * mm});
            skLineSegment(sketch, "E368", {"start": v(11.45, -3) * mm, "end": v(11.7, -3.58) * mm});
            skLineSegment(sketch, "E369", {"start": v(11.7, -3.58) * mm, "end": v(11.93, -4.16) * mm});
            skLineSegment(sketch, "E370", {"start": v(11.93, -4.16) * mm, "end": v(12.15, -4.74) * mm});
            skLineSegment(sketch, "E371", {"start": v(12.15, -4.74) * mm, "end": v(12.37, -5.32) * mm});
            skLineSegment(sketch, "E372", {"start": v(12.37, -5.32) * mm, "end": v(12.57, -5.89) * mm});
            skLineSegment(sketch, "E373", {"start": v(12.57, -5.89) * mm, "end": v(12.77, -6.46) * mm});
            skLineSegment(sketch, "E374", {"start": v(12.77, -6.46) * mm, "end": v(12.96, -7.03) * mm});
            skLineSegment(sketch, "E375", {"start": v(12.96, -7.03) * mm, "end": v(13.15, -7.6) * mm});
            skLineSegment(sketch, "E376", {"start": v(13.15, -7.6) * mm, "end": v(12.57, -7.73) * mm});
            skLineSegment(sketch, "E377", {"start": v(12.57, -7.73) * mm, "end": v(12, -7.86) * mm});
            skLineSegment(sketch, "E378", {"start": v(12, -7.86) * mm, "end": v(11.4, -7.97) * mm});
            skLineSegment(sketch, "E379", {"start": v(11.4, -7.97) * mm, "end": v(10.8, -8.08) * mm});
            skLineSegment(sketch, "E380", {"start": v(10.8, -8.08) * mm, "end": v(10.2, -8.18) * mm});
            skLineSegment(sketch, "E381", {"start": v(10.2, -8.18) * mm, "end": v(9.58, -8.28) * mm});
            skLineSegment(sketch, "E382", {"start": v(9.58, -8.28) * mm, "end": v(8.95, -8.37) * mm});
            skLineSegment(sketch, "E383", {"start": v(8.95, -8.37) * mm, "end": v(8.32, -8.45) * mm});
            skLineSegment(sketch, "E384", {"start": v(8.32, -8.45) * mm, "end": v(8.52, -8.13) * mm});
            skLineSegment(sketch, "E385", {"start": v(8.52, -8.13) * mm, "end": v(8.73, -7.8) * mm});
            skLineSegment(sketch, "E386", {"start": v(8.73, -7.8) * mm, "end": v(8.93, -7.48) * mm});
            skLineSegment(sketch, "E387", {"start": v(8.93, -7.48) * mm, "end": v(9.14, -7.14) * mm});
            skLineSegment(sketch, "E388", {"start": v(9.14, -7.14) * mm, "end": v(9.34, -6.8) * mm});
            skLineSegment(sketch, "E389", {"start": v(9.34, -6.8) * mm, "end": v(9.54, -6.47) * mm});
            skLineSegment(sketch, "E390", {"start": v(9.54, -6.47) * mm, "end": v(9.74, -6.12) * mm});
            skLineSegment(sketch, "E391", {"start": v(9.74, -6.12) * mm, "end": v(9.93, -5.77) * mm});
            skLineSegment(sketch, "E392", {"start": v(9.93, -5.77) * mm, "end": v(10.13, -5.42) * mm});
            skLineSegment(sketch, "E393", {"start": v(10.13, -5.42) * mm, "end": v(10.32, -5.07) * mm});
            skLineSegment(sketch, "E394", {"start": v(10.32, -5.07) * mm, "end": v(10.52, -4.72) * mm});
            skLineSegment(sketch, "E395", {"start": v(10.52, -4.72) * mm, "end": v(10.7, -4.37) * mm});
            skLineSegment(sketch, "E396", {"start": v(10.7, -4.37) * mm, "end": v(10.9, -4.02) * mm});
            skLineSegment(sketch, "E397", {"start": v(10.9, -4.02) * mm, "end": v(11.08, -3.67) * mm});
            skLineSegment(sketch, "E398", {"start": v(11.08, -3.67) * mm, "end": v(11.26, -3.33) * mm});
            skLineSegment(sketch, "E399", {"start": v(11.26, -3.33) * mm, "end": v(11.45, -3) * mm});
            skLineSegment(sketch, "E400", {"start": v(0, -15.12) * mm, "end": v(-0.4, -14.68) * mm});
            skLineSegment(sketch, "E401", {"start": v(-0.4, -14.68) * mm, "end": v(-0.8, -14.23) * mm});
            skLineSegment(sketch, "E402", {"start": v(-0.8, -14.23) * mm, "end": v(-1.19, -13.77) * mm});
            skLineSegment(sketch, "E403", {"start": v(-1.19, -13.77) * mm, "end": v(-1.58, -13.31) * mm});
            skLineSegment(sketch, "E404", {"start": v(-1.58, -13.31) * mm, "end": v(-1.96, -12.84) * mm});
            skLineSegment(sketch, "E405", {"start": v(-1.96, -12.84) * mm, "end": v(-2.34, -12.37) * mm});
            skLineSegment(sketch, "E406", {"start": v(-2.34, -12.37) * mm, "end": v(-2.71, -11.89) * mm});
            skLineSegment(sketch, "E407", {"start": v(-2.71, -11.89) * mm, "end": v(-3.09, -11.4) * mm});
            skLineSegment(sketch, "E408", {"start": v(-3.09, -11.4) * mm, "end": v(-2.7, -11.42) * mm});
            skLineSegment(sketch, "E409", {"start": v(-2.7, -11.42) * mm, "end": v(-2.31, -11.44) * mm});
            skLineSegment(sketch, "E410", {"start": v(-2.31, -11.44) * mm, "end": v(-1.93, -11.45) * mm});
            skLineSegment(sketch, "E411", {"start": v(-1.93, -11.45) * mm, "end": v(-1.54, -11.47) * mm});
            skLineSegment(sketch, "E412", {"start": v(-1.54, -11.47) * mm, "end": v(-1.16, -11.48) * mm});
            skLineSegment(sketch, "E413", {"start": v(-1.16, -11.48) * mm, "end": v(-0.77, -11.49) * mm});
            skLineSegment(sketch, "E414", {"start": v(-0.77, -11.49) * mm, "end": v(-0.39, -11.5) * mm});
            skLineSegment(sketch, "E415", {"start": v(-0.39, -11.5) * mm, "end": v(0, -11.5) * mm});
            skLineSegment(sketch, "E416", {"start": v(0, -11.5) * mm, "end": v(0.39, -11.5) * mm});
            skLineSegment(sketch, "E417", {"start": v(0.39, -11.5) * mm, "end": v(0.77, -11.49) * mm});
            skLineSegment(sketch, "E418", {"start": v(0.77, -11.49) * mm, "end": v(1.16, -11.48) * mm});
            skLineSegment(sketch, "E419", {"start": v(1.16, -11.48) * mm, "end": v(1.54, -11.47) * mm});
            skLineSegment(sketch, "E420", {"start": v(1.54, -11.47) * mm, "end": v(1.93, -11.45) * mm});
            skLineSegment(sketch, "E421", {"start": v(1.93, -11.45) * mm, "end": v(2.31, -11.44) * mm});
            skLineSegment(sketch, "E422", {"start": v(2.31, -11.44) * mm, "end": v(2.7, -11.42) * mm});
            skLineSegment(sketch, "E423", {"start": v(2.7, -11.42) * mm, "end": v(3.09, -11.4) * mm});
            skLineSegment(sketch, "E424", {"start": v(3.09, -11.4) * mm, "end": v(2.71, -11.89) * mm});
            skLineSegment(sketch, "E425", {"start": v(2.71, -11.89) * mm, "end": v(2.34, -12.37) * mm});
            skLineSegment(sketch, "E426", {"start": v(2.34, -12.37) * mm, "end": v(1.96, -12.84) * mm});
            skLineSegment(sketch, "E427", {"start": v(1.96, -12.84) * mm, "end": v(1.58, -13.31) * mm});
            skLineSegment(sketch, "E428", {"start": v(1.58, -13.31) * mm, "end": v(1.19, -13.77) * mm});
            skLineSegment(sketch, "E429", {"start": v(1.19, -13.77) * mm, "end": v(0.8, -14.23) * mm});
            skLineSegment(sketch, "E430", {"start": v(0.8, -14.23) * mm, "end": v(0.4, -14.68) * mm});
            skLineSegment(sketch, "E431", {"start": v(0.4, -14.68) * mm, "end": v(0, -15.12) * mm});
            skLineSegment(sketch, "E432", {"start": v(-8.32, -8.4) * mm, "end": v(-8.95, -8.32) * mm});
            skLineSegment(sketch, "E433", {"start": v(-8.95, -8.32) * mm, "end": v(-9.58, -8.23) * mm});
            skLineSegment(sketch, "E434", {"start": v(-9.58, -8.23) * mm, "end": v(-10.2, -8.14) * mm});
            skLineSegment(sketch, "E435", {"start": v(-10.2, -8.14) * mm, "end": v(-10.8, -8.03) * mm});
            skLineSegment(sketch, "E436", {"start": v(-10.8, -8.03) * mm, "end": v(-11.4, -7.93) * mm});
            skLineSegment(sketch, "E437", {"start": v(-11.4, -7.93) * mm, "end": v(-12, -7.81) * mm});
            skLineSegment(sketch, "E438", {"start": v(-12, -7.81) * mm, "end": v(-12.57, -7.69) * mm});
            skLineSegment(sketch, "E439", {"start": v(-12.57, -7.69) * mm, "end": v(-13.15, -7.56) * mm});
            skLineSegment(sketch, "E440", {"start": v(-13.15, -7.56) * mm, "end": v(-12.96, -7) * mm});
            skLineSegment(sketch, "E441", {"start": v(-12.96, -7) * mm, "end": v(-12.77, -6.44) * mm});
            skLineSegment(sketch, "E442", {"start": v(-12.77, -6.44) * mm, "end": v(-12.57, -5.86) * mm});
            skLineSegment(sketch, "E443", {"start": v(-12.57, -5.86) * mm, "end": v(-12.37, -5.29) * mm});
            skLineSegment(sketch, "E444", {"start": v(-12.37, -5.29) * mm, "end": v(-12.15, -4.7) * mm});
            skLineSegment(sketch, "E445", {"start": v(-12.15, -4.7) * mm, "end": v(-11.93, -4.12) * mm});
            skLineSegment(sketch, "E446", {"start": v(-11.93, -4.12) * mm, "end": v(-11.7, -3.54) * mm});
            skLineSegment(sketch, "E447", {"start": v(-11.7, -3.54) * mm, "end": v(-11.45, -2.95) * mm});
            skLineSegment(sketch, "E448", {"start": v(-11.45, -2.95) * mm, "end": v(-11.26, -3.29) * mm});
            skLineSegment(sketch, "E449", {"start": v(-11.26, -3.29) * mm, "end": v(-11.08, -3.63) * mm});
            skLineSegment(sketch, "E450", {"start": v(-11.08, -3.63) * mm, "end": v(-10.9, -3.97) * mm});
            skLineSegment(sketch, "E451", {"start": v(-10.9, -3.97) * mm, "end": v(-10.7, -4.32) * mm});
            skLineSegment(sketch, "E452", {"start": v(-10.7, -4.32) * mm, "end": v(-10.52, -4.66) * mm});
            skLineSegment(sketch, "E453", {"start": v(-10.52, -4.66) * mm, "end": v(-10.32, -5) * mm});
            skLineSegment(sketch, "E454", {"start": v(-10.32, -5) * mm, "end": v(-10.13, -5.34) * mm});
            skLineSegment(sketch, "E455", {"start": v(-10.13, -5.34) * mm, "end": v(-9.93, -5.68) * mm});
            skLineSegment(sketch, "E456", {"start": v(-9.93, -5.68) * mm, "end": v(-9.73, -6.04) * mm});
            skLineSegment(sketch, "E457", {"start": v(-9.73, -6.04) * mm, "end": v(-9.53, -6.4) * mm});
            skLineSegment(sketch, "E458", {"start": v(-9.53, -6.4) * mm, "end": v(-9.32, -6.74) * mm});
            skLineSegment(sketch, "E459", {"start": v(-9.32, -6.74) * mm, "end": v(-9.12, -7.08) * mm});
            skLineSegment(sketch, "E460", {"start": v(-9.12, -7.08) * mm, "end": v(-8.92, -7.41) * mm});
            skLineSegment(sketch, "E461", {"start": v(-8.92, -7.41) * mm, "end": v(-8.72, -7.74) * mm});
            skLineSegment(sketch, "E462", {"start": v(-8.72, -7.74) * mm, "end": v(-8.52, -8.07) * mm});
            skLineSegment(sketch, "E463", {"start": v(-8.52, -8.07) * mm, "end": v(-8.32, -8.4) * mm});
            skLineSegment(sketch, "E464", {"start": v(-11.45, 3) * mm, "end": v(-11.7, 3.58) * mm});
            skLineSegment(sketch, "E465", {"start": v(-11.7, 3.58) * mm, "end": v(-11.93, 4.16) * mm});
            skLineSegment(sketch, "E466", {"start": v(-11.93, 4.16) * mm, "end": v(-12.15, 4.74) * mm});
            skLineSegment(sketch, "E467", {"start": v(-12.15, 4.74) * mm, "end": v(-12.37, 5.32) * mm});
            skLineSegment(sketch, "E468", {"start": v(-12.37, 5.32) * mm, "end": v(-12.57, 5.89) * mm});
            skLineSegment(sketch, "E469", {"start": v(-12.57, 5.89) * mm, "end": v(-12.77, 6.46) * mm});
            skLineSegment(sketch, "E470", {"start": v(-12.77, 6.46) * mm, "end": v(-12.96, 7.03) * mm});
            skLineSegment(sketch, "E471", {"start": v(-12.96, 7.03) * mm, "end": v(-13.15, 7.6) * mm});
            skLineSegment(sketch, "E472", {"start": v(-13.15, 7.6) * mm, "end": v(-12.57, 7.73) * mm});
            skLineSegment(sketch, "E473", {"start": v(-12.57, 7.73) * mm, "end": v(-12, 7.86) * mm});
            skLineSegment(sketch, "E474", {"start": v(-12, 7.86) * mm, "end": v(-11.4, 7.97) * mm});
            skLineSegment(sketch, "E475", {"start": v(-11.4, 7.97) * mm, "end": v(-10.8, 8.08) * mm});
            skLineSegment(sketch, "E476", {"start": v(-10.8, 8.08) * mm, "end": v(-10.2, 8.18) * mm});
            skLineSegment(sketch, "E477", {"start": v(-10.2, 8.18) * mm, "end": v(-9.58, 8.28) * mm});
            skLineSegment(sketch, "E478", {"start": v(-9.58, 8.28) * mm, "end": v(-8.95, 8.37) * mm});
            skLineSegment(sketch, "E479", {"start": v(-8.95, 8.37) * mm, "end": v(-8.32, 8.45) * mm});
            skLineSegment(sketch, "E480", {"start": v(-8.32, 8.45) * mm, "end": v(-8.52, 8.13) * mm});
            skLineSegment(sketch, "E481", {"start": v(-8.52, 8.13) * mm, "end": v(-8.73, 7.8) * mm});
            skLineSegment(sketch, "E482", {"start": v(-8.73, 7.8) * mm, "end": v(-8.93, 7.48) * mm});
            skLineSegment(sketch, "E483", {"start": v(-8.93, 7.48) * mm, "end": v(-9.14, 7.14) * mm});
            skLineSegment(sketch, "E484", {"start": v(-9.14, 7.14) * mm, "end": v(-9.34, 6.8) * mm});
            skLineSegment(sketch, "E485", {"start": v(-9.34, 6.8) * mm, "end": v(-9.54, 6.47) * mm});
            skLineSegment(sketch, "E486", {"start": v(-9.54, 6.47) * mm, "end": v(-9.74, 6.12) * mm});
            skLineSegment(sketch, "E487", {"start": v(-9.74, 6.12) * mm, "end": v(-9.93, 5.77) * mm});
            skLineSegment(sketch, "E488", {"start": v(-9.93, 5.77) * mm, "end": v(-10.13, 5.42) * mm});
            skLineSegment(sketch, "E489", {"start": v(-10.13, 5.42) * mm, "end": v(-10.32, 5.07) * mm});
            skLineSegment(sketch, "E490", {"start": v(-10.32, 5.07) * mm, "end": v(-10.52, 4.72) * mm});
            skLineSegment(sketch, "E491", {"start": v(-10.52, 4.72) * mm, "end": v(-10.7, 4.37) * mm});
            skLineSegment(sketch, "E492", {"start": v(-10.7, 4.37) * mm, "end": v(-10.9, 4.02) * mm});
            skLineSegment(sketch, "E493", {"start": v(-10.9, 4.02) * mm, "end": v(-11.08, 3.67) * mm});
            skLineSegment(sketch, "E494", {"start": v(-11.08, 3.67) * mm, "end": v(-11.26, 3.33) * mm});
            skLineSegment(sketch, "E495", {"start": v(-11.26, 3.33) * mm, "end": v(-11.45, 3) * mm});
            skLineSegment(sketch, "E496", {"start": v(0, 15.12) * mm, "end": v(0.4, 14.68) * mm});
            skLineSegment(sketch, "E497", {"start": v(0.4, 14.68) * mm, "end": v(0.8, 14.23) * mm});
            skLineSegment(sketch, "E498", {"start": v(0.8, 14.23) * mm, "end": v(1.19, 13.77) * mm});
            skLineSegment(sketch, "E499", {"start": v(1.19, 13.77) * mm, "end": v(1.58, 13.31) * mm});
            skLineSegment(sketch, "E500", {"start": v(1.58, 13.31) * mm, "end": v(1.96, 12.84) * mm});
            skLineSegment(sketch, "E501", {"start": v(1.96, 12.84) * mm, "end": v(2.34, 12.37) * mm});
            skLineSegment(sketch, "E502", {"start": v(2.34, 12.37) * mm, "end": v(2.71, 11.89) * mm});
            skLineSegment(sketch, "E503", {"start": v(2.71, 11.89) * mm, "end": v(3.09, 11.4) * mm});
            skLineSegment(sketch, "E504", {"start": v(3.09, 11.4) * mm, "end": v(2.7, 11.42) * mm});
            skLineSegment(sketch, "E505", {"start": v(2.7, 11.42) * mm, "end": v(2.31, 11.44) * mm});
            skLineSegment(sketch, "E506", {"start": v(2.31, 11.44) * mm, "end": v(1.93, 11.45) * mm});
            skLineSegment(sketch, "E507", {"start": v(1.93, 11.45) * mm, "end": v(1.54, 11.47) * mm});
            skLineSegment(sketch, "E508", {"start": v(1.54, 11.47) * mm, "end": v(1.16, 11.48) * mm});
            skLineSegment(sketch, "E509", {"start": v(1.16, 11.48) * mm, "end": v(0.77, 11.49) * mm});
            skLineSegment(sketch, "E510", {"start": v(0.77, 11.49) * mm, "end": v(0.39, 11.5) * mm});
            skLineSegment(sketch, "E511", {"start": v(0.39, 11.5) * mm, "end": v(0, 11.5) * mm});
            skLineSegment(sketch, "E512", {"start": v(0, 11.5) * mm, "end": v(-0.39, 11.5) * mm});
            skLineSegment(sketch, "E513", {"start": v(-0.39, 11.5) * mm, "end": v(-0.77, 11.49) * mm});
            skLineSegment(sketch, "E514", {"start": v(-0.77, 11.49) * mm, "end": v(-1.16, 11.48) * mm});
            skLineSegment(sketch, "E515", {"start": v(-1.16, 11.48) * mm, "end": v(-1.54, 11.47) * mm});
            skLineSegment(sketch, "E516", {"start": v(-1.54, 11.47) * mm, "end": v(-1.93, 11.45) * mm});
            skLineSegment(sketch, "E517", {"start": v(-1.93, 11.45) * mm, "end": v(-2.31, 11.44) * mm});
            skLineSegment(sketch, "E518", {"start": v(-2.31, 11.44) * mm, "end": v(-2.7, 11.42) * mm});
            skLineSegment(sketch, "E519", {"start": v(-2.7, 11.42) * mm, "end": v(-3.09, 11.4) * mm});
            skLineSegment(sketch, "E520", {"start": v(-3.09, 11.4) * mm, "end": v(-2.71, 11.89) * mm});
            skLineSegment(sketch, "E521", {"start": v(-2.71, 11.89) * mm, "end": v(-2.34, 12.37) * mm});
            skLineSegment(sketch, "E522", {"start": v(-2.34, 12.37) * mm, "end": v(-1.96, 12.84) * mm});
            skLineSegment(sketch, "E523", {"start": v(-1.96, 12.84) * mm, "end": v(-1.58, 13.31) * mm});
            skLineSegment(sketch, "E524", {"start": v(-1.58, 13.31) * mm, "end": v(-1.19, 13.77) * mm});
            skLineSegment(sketch, "E525", {"start": v(-1.19, 13.77) * mm, "end": v(-0.8, 14.23) * mm});
            skLineSegment(sketch, "E526", {"start": v(-0.8, 14.23) * mm, "end": v(-0.4, 14.68) * mm});
            skLineSegment(sketch, "E527", {"start": v(-0.4, 14.68) * mm, "end": v(0, 15.12) * mm});
            skLineSegment(sketch, "E528", {"start": v(9.93, 5.72) * mm, "end": v(9.73, 6.06) * mm});
            skLineSegment(sketch, "E529", {"start": v(9.73, 6.06) * mm, "end": v(9.53, 6.4) * mm});
            skLineSegment(sketch, "E530", {"start": v(9.53, 6.4) * mm, "end": v(9.32, 6.73) * mm});
            skLineSegment(sketch, "E531", {"start": v(9.32, 6.73) * mm, "end": v(9.12, 7.07) * mm});
            skLineSegment(sketch, "E532", {"start": v(9.12, 7.07) * mm, "end": v(8.92, 7.4) * mm});
            skLineSegment(sketch, "E533", {"start": v(8.92, 7.4) * mm, "end": v(8.72, 7.74) * mm});
            skLineSegment(sketch, "E534", {"start": v(8.72, 7.74) * mm, "end": v(8.52, 8.07) * mm});
            skLineSegment(sketch, "E535", {"start": v(8.52, 8.07) * mm, "end": v(8.32, 8.4) * mm});
            skLineSegment(sketch, "E536", {"start": v(8.32, 8.4) * mm, "end": v(8.95, 8.32) * mm});
            skLineSegment(sketch, "E537", {"start": v(8.95, 8.32) * mm, "end": v(9.58, 8.23) * mm});
            skLineSegment(sketch, "E538", {"start": v(9.58, 8.23) * mm, "end": v(10.2, 8.14) * mm});
            skLineSegment(sketch, "E539", {"start": v(10.2, 8.14) * mm, "end": v(10.8, 8.03) * mm});
            skLineSegment(sketch, "E540", {"start": v(10.8, 8.03) * mm, "end": v(11.4, 7.93) * mm});
            skLineSegment(sketch, "E541", {"start": v(11.4, 7.93) * mm, "end": v(12, 7.81) * mm});
            skLineSegment(sketch, "E542", {"start": v(12, 7.81) * mm, "end": v(12.57, 7.69) * mm});
            skLineSegment(sketch, "E543", {"start": v(12.57, 7.69) * mm, "end": v(13.15, 7.56) * mm});
            skLineSegment(sketch, "E544", {"start": v(13.15, 7.56) * mm, "end": v(12.96, 7) * mm});
            skLineSegment(sketch, "E545", {"start": v(12.96, 7) * mm, "end": v(12.77, 6.44) * mm});
            skLineSegment(sketch, "E546", {"start": v(12.77, 6.44) * mm, "end": v(12.57, 5.86) * mm});
            skLineSegment(sketch, "E547", {"start": v(12.57, 5.86) * mm, "end": v(12.37, 5.29) * mm});
            skLineSegment(sketch, "E548", {"start": v(12.37, 5.29) * mm, "end": v(12.15, 4.7) * mm});
            skLineSegment(sketch, "E549", {"start": v(12.15, 4.7) * mm, "end": v(11.93, 4.12) * mm});
            skLineSegment(sketch, "E550", {"start": v(11.93, 4.12) * mm, "end": v(11.7, 3.54) * mm});
            skLineSegment(sketch, "E551", {"start": v(11.7, 3.54) * mm, "end": v(11.45, 2.95) * mm});
            skLineSegment(sketch, "E552", {"start": v(11.45, 2.95) * mm, "end": v(11.26, 3.3) * mm});
            skLineSegment(sketch, "E553", {"start": v(11.26, 3.3) * mm, "end": v(11.08, 3.66) * mm});
            skLineSegment(sketch, "E554", {"start": v(11.08, 3.66) * mm, "end": v(10.9, 4) * mm});
            skLineSegment(sketch, "E555", {"start": v(10.9, 4) * mm, "end": v(10.7, 4.35) * mm});
            skLineSegment(sketch, "E556", {"start": v(10.7, 4.35) * mm, "end": v(10.52, 4.7) * mm});
            skLineSegment(sketch, "E557", {"start": v(10.52, 4.7) * mm, "end": v(10.32, 5.05) * mm});
            skLineSegment(sketch, "E558", {"start": v(10.32, 5.05) * mm, "end": v(10.13, 5.39) * mm});
            skLineSegment(sketch, "E559", {"start": v(10.13, 5.39) * mm, "end": v(9.93, 5.72) * mm});
            skLineSegment(sketch, "E560", {"start": v(-14.45, 12.97) * mm, "end": v(-14.67, 14.66) * mm});
            skLineSegment(sketch, "E561", {"start": v(-14.67, 14.66) * mm, "end": v(-14.76, 16.22) * mm});
            skLineSegment(sketch, "E562", {"start": v(-14.76, 16.22) * mm, "end": v(-14.73, 17.62) * mm});
            skLineSegment(sketch, "E563", {"start": v(-14.73, 17.62) * mm, "end": v(-14.57, 18.87) * mm});
            skLineSegment(sketch, "E564", {"start": v(-14.57, 18.87) * mm, "end": v(-14.29, 19.94) * mm});
            skLineSegment(sketch, "E565", {"start": v(-14.29, 19.94) * mm, "end": v(-13.9, 20.84) * mm});
            skLineSegment(sketch, "E566", {"start": v(-13.9, 20.84) * mm, "end": v(-13.38, 21.54) * mm});
            skLineSegment(sketch, "E567", {"start": v(-13.38, 21.54) * mm, "end": v(-12.75, 22.05) * mm});
            skLineSegment(sketch, "E568", {"start": v(-12.75, 22.05) * mm, "end": v(-12.57, 22.14) * mm});
            skLineSegment(sketch, "E569", {"start": v(-12.57, 22.14) * mm, "end": v(-12.4, 22.22) * mm});
            skLineSegment(sketch, "E570", {"start": v(-12.4, 22.22) * mm, "end": v(-12.2, 22.3) * mm});
            skLineSegment(sketch, "E571", {"start": v(-12.2, 22.3) * mm, "end": v(-12.01, 22.35) * mm});
            skLineSegment(sketch, "E572", {"start": v(-12.01, 22.35) * mm, "end": v(-11.81, 22.4) * mm});
            skLineSegment(sketch, "E573", {"start": v(-11.81, 22.4) * mm, "end": v(-11.6, 22.43) * mm});
            skLineSegment(sketch, "E574", {"start": v(-11.6, 22.43) * mm, "end": v(-11.4, 22.44) * mm});
            skLineSegment(sketch, "E575", {"start": v(-11.4, 22.44) * mm, "end": v(-11.18, 22.45) * mm});
            skLineSegment(sketch, "E576", {"start": v(-11.18, 22.45) * mm, "end": v(-10.14, 22.35) * mm});
            skLineSegment(sketch, "E577", {"start": v(-10.14, 22.35) * mm, "end": v(-9.05, 22.06) * mm});
            skLineSegment(sketch, "E578", {"start": v(-9.05, 22.06) * mm, "end": v(-7.91, 21.58) * mm});
            skLineSegment(sketch, "E579", {"start": v(-7.91, 21.58) * mm, "end": v(-6.74, 20.94) * mm});
            skLineSegment(sketch, "E580", {"start": v(-6.74, 20.94) * mm, "end": v(-5.53, 20.14) * mm});
            skLineSegment(sketch, "E581", {"start": v(-5.53, 20.14) * mm, "end": v(-4.3, 19.2) * mm});
            skLineSegment(sketch, "E582", {"start": v(-4.3, 19.2) * mm, "end": v(-3.05, 18.14) * mm});
            skLineSegment(sketch, "E583", {"start": v(-3.05, 18.14) * mm, "end": v(-1.79, 16.95) * mm});
            skLineSegment(sketch, "E584", {"start": v(-1.79, 16.95) * mm, "end": v(-2.38, 16.3) * mm});
            skLineSegment(sketch, "E585", {"start": v(-2.38, 16.3) * mm, "end": v(-2.96, 15.63) * mm});
            skLineSegment(sketch, "E586", {"start": v(-2.96, 15.63) * mm, "end": v(-3.55, 14.93) * mm});
            skLineSegment(sketch, "E587", {"start": v(-3.55, 14.93) * mm, "end": v(-4.13, 14.21) * mm});
            skLineSegment(sketch, "E588", {"start": v(-4.13, 14.21) * mm, "end": v(-4.71, 13.47) * mm});
            skLineSegment(sketch, "E589", {"start": v(-4.71, 13.47) * mm, "end": v(-5.3, 12.71) * mm});
            skLineSegment(sketch, "E590", {"start": v(-5.3, 12.71) * mm, "end": v(-5.87, 11.93) * mm});
            skLineSegment(sketch, "E591", {"start": v(-5.87, 11.93) * mm, "end": v(-6.44, 11.14) * mm});
            skLineSegment(sketch, "E592", {"start": v(-6.44, 11.14) * mm, "end": v(-7.4, 11.04) * mm});
            skLineSegment(sketch, "E593", {"start": v(-7.4, 11.04) * mm, "end": v(-8.36, 10.94) * mm});
            skLineSegment(sketch, "E594", {"start": v(-8.36, 10.94) * mm, "end": v(-9.3, 10.81) * mm});
            skLineSegment(sketch, "E595", {"start": v(-9.3, 10.81) * mm, "end": v(-10.23, 10.68) * mm});
            skLineSegment(sketch, "E596", {"start": v(-10.23, 10.68) * mm, "end": v(-11.15, 10.53) * mm});
            skLineSegment(sketch, "E597", {"start": v(-11.15, 10.53) * mm, "end": v(-12.05, 10.37) * mm});
            skLineSegment(sketch, "E598", {"start": v(-12.05, 10.37) * mm, "end": v(-12.94, 10.2) * mm});
            skLineSegment(sketch, "E599", {"start": v(-12.94, 10.2) * mm, "end": v(-13.82, 10.02) * mm});
            skLineSegment(sketch, "E600", {"start": v(-13.82, 10.02) * mm, "end": v(-13.92, 10.4) * mm});
            skLineSegment(sketch, "E601", {"start": v(-13.92, 10.4) * mm, "end": v(-14, 10.78) * mm});
            skLineSegment(sketch, "E602", {"start": v(-14, 10.78) * mm, "end": v(-14.09, 11.16) * mm});
            skLineSegment(sketch, "E603", {"start": v(-14.09, 11.16) * mm, "end": v(-14.17, 11.53) * mm});
            skLineSegment(sketch, "E604", {"start": v(-14.17, 11.53) * mm, "end": v(-14.24, 11.9) * mm});
            skLineSegment(sketch, "E605", {"start": v(-14.24, 11.9) * mm, "end": v(-14.3, 12.26) * mm});
            skLineSegment(sketch, "E606", {"start": v(-14.3, 12.26) * mm, "end": v(-14.38, 12.62) * mm});
            skLineSegment(sketch, "E607", {"start": v(-14.38, 12.62) * mm, "end": v(-14.45, 12.97) * mm});
            skLineSegment(sketch, "E608", {"start": v(-25.5, 0) * mm, "end": v(-25.37, 0.8) * mm});
            skLineSegment(sketch, "E609", {"start": v(-25.37, 0.8) * mm, "end": v(-25.02, 1.6) * mm});
            skLineSegment(sketch, "E610", {"start": v(-25.02, 1.6) * mm, "end": v(-24.45, 2.38) * mm});
            skLineSegment(sketch, "E611", {"start": v(-24.45, 2.38) * mm, "end": v(-23.66, 3.16) * mm});
            skLineSegment(sketch, "E612", {"start": v(-23.66, 3.16) * mm, "end": v(-22.66, 3.92) * mm});
            skLineSegment(sketch, "E613", {"start": v(-22.66, 3.92) * mm, "end": v(-21.45, 4.65) * mm});
            skLineSegment(sketch, "E614", {"start": v(-21.45, 4.65) * mm, "end": v(-20.06, 5.35) * mm});
            skLineSegment(sketch, "E615", {"start": v(-20.06, 5.35) * mm, "end": v(-18.47, 6) * mm});
            skLineSegment(sketch, "E616", {"start": v(-18.47, 6) * mm, "end": v(-18.13, 6.12) * mm});
            skLineSegment(sketch, "E617", {"start": v(-18.13, 6.12) * mm, "end": v(-17.78, 6.25) * mm});
            skLineSegment(sketch, "E618", {"start": v(-17.78, 6.25) * mm, "end": v(-17.43, 6.38) * mm});
            skLineSegment(sketch, "E619", {"start": v(-17.43, 6.38) * mm, "end": v(-17.07, 6.5) * mm});
            skLineSegment(sketch, "E620", {"start": v(-17.07, 6.5) * mm, "end": v(-16.71, 6.61) * mm});
            skLineSegment(sketch, "E621", {"start": v(-16.71, 6.61) * mm, "end": v(-16.34, 6.72) * mm});
            skLineSegment(sketch, "E622", {"start": v(-16.34, 6.72) * mm, "end": v(-15.98, 6.83) * mm});
            skLineSegment(sketch, "E623", {"start": v(-15.98, 6.83) * mm, "end": v(-15.6, 6.93) * mm});
            skLineSegment(sketch, "E624", {"start": v(-15.6, 6.93) * mm, "end": v(-15.33, 6.09) * mm});
            skLineSegment(sketch, "E625", {"start": v(-15.33, 6.09) * mm, "end": v(-15.04, 5.23) * mm});
            skLineSegment(sketch, "E626", {"start": v(-15.04, 5.23) * mm, "end": v(-14.73, 4.37) * mm});
            skLineSegment(sketch, "E627", {"start": v(-14.73, 4.37) * mm, "end": v(-14.4, 3.5) * mm});
            skLineSegment(sketch, "E628", {"start": v(-14.4, 3.5) * mm, "end": v(-14.06, 2.61) * mm});
            skLineSegment(sketch, "E629", {"start": v(-14.06, 2.61) * mm, "end": v(-13.7, 1.73) * mm});
            skLineSegment(sketch, "E630", {"start": v(-13.7, 1.73) * mm, "end": v(-13.32, 0.84) * mm});
            skLineSegment(sketch, "E631", {"start": v(-13.32, 0.84) * mm, "end": v(-12.92, -0.04) * mm});
            skLineSegment(sketch, "E632", {"start": v(-12.92, -0.04) * mm, "end": v(-13.32, -0.93) * mm});
            skLineSegment(sketch, "E633", {"start": v(-13.32, -0.93) * mm, "end": v(-13.7, -1.81) * mm});
            skLineSegment(sketch, "E634", {"start": v(-13.7, -1.81) * mm, "end": v(-14.07, -2.7) * mm});
            skLineSegment(sketch, "E635", {"start": v(-14.07, -2.7) * mm, "end": v(-14.42, -3.56) * mm});
            skLineSegment(sketch, "E636", {"start": v(-14.42, -3.56) * mm, "end": v(-14.75, -4.43) * mm});
            skLineSegment(sketch, "E637", {"start": v(-14.75, -4.43) * mm, "end": v(-15.06, -5.28) * mm});
            skLineSegment(sketch, "E638", {"start": v(-15.06, -5.28) * mm, "end": v(-15.34, -6.13) * mm});
            skLineSegment(sketch, "E639", {"start": v(-15.34, -6.13) * mm, "end": v(-15.6, -6.98) * mm});
            skLineSegment(sketch, "E640", {"start": v(-15.6, -6.98) * mm, "end": v(-17.8, -6.27) * mm});
            skLineSegment(sketch, "E641", {"start": v(-17.8, -6.27) * mm, "end": v(-19.76, -5.48) * mm});
            skLineSegment(sketch, "E642", {"start": v(-19.76, -5.48) * mm, "end": v(-21.45, -4.64) * mm});
            skLineSegment(sketch, "E643", {"start": v(-21.45, -4.64) * mm, "end": v(-22.86, -3.76) * mm});
            skLineSegment(sketch, "E644", {"start": v(-22.86, -3.76) * mm, "end": v(-24, -2.84) * mm});
            skLineSegment(sketch, "E645", {"start": v(-24, -2.84) * mm, "end": v(-24.82, -1.9) * mm});
            skLineSegment(sketch, "E646", {"start": v(-24.82, -1.9) * mm, "end": v(-25.32, -0.95) * mm});
            skLineSegment(sketch, "E647", {"start": v(-25.32, -0.95) * mm, "end": v(-25.5, 0) * mm});
            skLineSegment(sketch, "E648", {"start": v(-12.75, -22.05) * mm, "end": v(-13.38, -21.54) * mm});
            skLineSegment(sketch, "E649", {"start": v(-13.38, -21.54) * mm, "end": v(-13.9, -20.84) * mm});
            skLineSegment(sketch, "E650", {"start": v(-13.9, -20.84) * mm, "end": v(-14.29, -19.94) * mm});
            skLineSegment(sketch, "E651", {"start": v(-14.29, -19.94) * mm, "end": v(-14.57, -18.87) * mm});
            skLineSegment(sketch, "E652", {"start": v(-14.57, -18.87) * mm, "end": v(-14.73, -17.62) * mm});
            skLineSegment(sketch, "E653", {"start": v(-14.73, -17.62) * mm, "end": v(-14.76, -16.22) * mm});
            skLineSegment(sketch, "E654", {"start": v(-14.76, -16.22) * mm, "end": v(-14.67, -14.66) * mm});
            skLineSegment(sketch, "E655", {"start": v(-14.67, -14.66) * mm, "end": v(-14.45, -12.97) * mm});
            skLineSegment(sketch, "E656", {"start": v(-14.45, -12.97) * mm, "end": v(-14.4, -12.62) * mm});
            skLineSegment(sketch, "E657", {"start": v(-14.4, -12.62) * mm, "end": v(-14.33, -12.26) * mm});
            skLineSegment(sketch, "E658", {"start": v(-14.33, -12.26) * mm, "end": v(-14.26, -11.9) * mm});
            skLineSegment(sketch, "E659", {"start": v(-14.26, -11.9) * mm, "end": v(-14.18, -11.53) * mm});
            skLineSegment(sketch, "E660", {"start": v(-14.18, -11.53) * mm, "end": v(-14.1, -11.16) * mm});
            skLineSegment(sketch, "E661", {"start": v(-14.1, -11.16) * mm, "end": v(-14.01, -10.78) * mm});
            skLineSegment(sketch, "E662", {"start": v(-14.01, -10.78) * mm, "end": v(-13.92, -10.4) * mm});
            skLineSegment(sketch, "E663", {"start": v(-13.92, -10.4) * mm, "end": v(-13.82, -10.02) * mm});
            skLineSegment(sketch, "E664", {"start": v(-13.82, -10.02) * mm, "end": v(-12.94, -10.21) * mm});
            skLineSegment(sketch, "E665", {"start": v(-12.94, -10.21) * mm, "end": v(-12.05, -10.39) * mm});
            skLineSegment(sketch, "E666", {"start": v(-12.05, -10.39) * mm, "end": v(-11.15, -10.55) * mm});
            skLineSegment(sketch, "E667", {"start": v(-11.15, -10.55) * mm, "end": v(-10.23, -10.7) * mm});
            skLineSegment(sketch, "E668", {"start": v(-10.23, -10.7) * mm, "end": v(-9.3, -10.83) * mm});
            skLineSegment(sketch, "E669", {"start": v(-9.3, -10.83) * mm, "end": v(-8.36, -10.94) * mm});
            skLineSegment(sketch, "E670", {"start": v(-8.36, -10.94) * mm, "end": v(-7.4, -11.05) * mm});
            skLineSegment(sketch, "E671", {"start": v(-7.4, -11.05) * mm, "end": v(-6.44, -11.14) * mm});
            skLineSegment(sketch, "E672", {"start": v(-6.44, -11.14) * mm, "end": v(-5.87, -11.93) * mm});
            skLineSegment(sketch, "E673", {"start": v(-5.87, -11.93) * mm, "end": v(-5.3, -12.7) * mm});
            skLineSegment(sketch, "E674", {"start": v(-5.3, -12.7) * mm, "end": v(-4.71, -13.46) * mm});
            skLineSegment(sketch, "E675", {"start": v(-4.71, -13.46) * mm, "end": v(-4.13, -14.2) * mm});
            skLineSegment(sketch, "E676", {"start": v(-4.13, -14.2) * mm, "end": v(-3.55, -14.9) * mm});
            skLineSegment(sketch, "E677", {"start": v(-3.55, -14.9) * mm, "end": v(-2.96, -15.6) * mm});
            skLineSegment(sketch, "E678", {"start": v(-2.96, -15.6) * mm, "end": v(-2.38, -16.29) * mm});
            skLineSegment(sketch, "E679", {"start": v(-2.38, -16.29) * mm, "end": v(-1.79, -16.95) * mm});
            skLineSegment(sketch, "E680", {"start": v(-1.79, -16.95) * mm, "end": v(-3.03, -18.12) * mm});
            skLineSegment(sketch, "E681", {"start": v(-3.03, -18.12) * mm, "end": v(-4.27, -19.19) * mm});
            skLineSegment(sketch, "E682", {"start": v(-4.27, -19.19) * mm, "end": v(-5.5, -20.13) * mm});
            skLineSegment(sketch, "E683", {"start": v(-5.5, -20.13) * mm, "end": v(-6.7, -20.92) * mm});
            skLineSegment(sketch, "E684", {"start": v(-6.7, -20.92) * mm, "end": v(-7.88, -21.57) * mm});
            skLineSegment(sketch, "E685", {"start": v(-7.88, -21.57) * mm, "end": v(-9.03, -22.05) * mm});
            skLineSegment(sketch, "E686", {"start": v(-9.03, -22.05) * mm, "end": v(-10.13, -22.35) * mm});
            skLineSegment(sketch, "E687", {"start": v(-10.13, -22.35) * mm, "end": v(-11.18, -22.45) * mm});
            skLineSegment(sketch, "E688", {"start": v(-11.18, -22.45) * mm, "end": v(-11.4, -22.44) * mm});
            skLineSegment(sketch, "E689", {"start": v(-11.4, -22.44) * mm, "end": v(-11.6, -22.43) * mm});
            skLineSegment(sketch, "E690", {"start": v(-11.6, -22.43) * mm, "end": v(-11.81, -22.4) * mm});
            skLineSegment(sketch, "E691", {"start": v(-11.81, -22.4) * mm, "end": v(-12.01, -22.35) * mm});
            skLineSegment(sketch, "E692", {"start": v(-12.01, -22.35) * mm, "end": v(-12.2, -22.3) * mm});
            skLineSegment(sketch, "E693", {"start": v(-12.2, -22.3) * mm, "end": v(-12.4, -22.22) * mm});
            skLineSegment(sketch, "E694", {"start": v(-12.4, -22.22) * mm, "end": v(-12.57, -22.14) * mm});
            skLineSegment(sketch, "E695", {"start": v(-12.57, -22.14) * mm, "end": v(-12.75, -22.05) * mm});
            skLineSegment(sketch, "E696", {"start": v(14.45, -12.97) * mm, "end": v(14.67, -14.66) * mm});
            skLineSegment(sketch, "E697", {"start": v(14.67, -14.66) * mm, "end": v(14.76, -16.22) * mm});
            skLineSegment(sketch, "E698", {"start": v(14.76, -16.22) * mm, "end": v(14.73, -17.62) * mm});
            skLineSegment(sketch, "E699", {"start": v(14.73, -17.62) * mm, "end": v(14.57, -18.87) * mm});
            skLineSegment(sketch, "E700", {"start": v(14.57, -18.87) * mm, "end": v(14.29, -19.94) * mm});
            skLineSegment(sketch, "E701", {"start": v(14.29, -19.94) * mm, "end": v(13.9, -20.84) * mm});
            skLineSegment(sketch, "E702", {"start": v(13.9, -20.84) * mm, "end": v(13.38, -21.54) * mm});
            skLineSegment(sketch, "E703", {"start": v(13.38, -21.54) * mm, "end": v(12.75, -22.05) * mm});
            skLineSegment(sketch, "E704", {"start": v(12.75, -22.05) * mm, "end": v(12.57, -22.14) * mm});
            skLineSegment(sketch, "E705", {"start": v(12.57, -22.14) * mm, "end": v(12.4, -22.22) * mm});
            skLineSegment(sketch, "E706", {"start": v(12.4, -22.22) * mm, "end": v(12.2, -22.3) * mm});
            skLineSegment(sketch, "E707", {"start": v(12.2, -22.3) * mm, "end": v(12.01, -22.35) * mm});
            skLineSegment(sketch, "E708", {"start": v(12.01, -22.35) * mm, "end": v(11.81, -22.4) * mm});
            skLineSegment(sketch, "E709", {"start": v(11.81, -22.4) * mm, "end": v(11.6, -22.43) * mm});
            skLineSegment(sketch, "E710", {"start": v(11.6, -22.43) * mm, "end": v(11.4, -22.44) * mm});
            skLineSegment(sketch, "E711", {"start": v(11.4, -22.44) * mm, "end": v(11.18, -22.45) * mm});
            skLineSegment(sketch, "E712", {"start": v(11.18, -22.45) * mm, "end": v(10.14, -22.35) * mm});
            skLineSegment(sketch, "E713", {"start": v(10.14, -22.35) * mm, "end": v(9.05, -22.06) * mm});
            skLineSegment(sketch, "E714", {"start": v(9.05, -22.06) * mm, "end": v(7.91, -21.58) * mm});
            skLineSegment(sketch, "E715", {"start": v(7.91, -21.58) * mm, "end": v(6.74, -20.94) * mm});
            skLineSegment(sketch, "E716", {"start": v(6.74, -20.94) * mm, "end": v(5.53, -20.14) * mm});
            skLineSegment(sketch, "E717", {"start": v(5.53, -20.14) * mm, "end": v(4.3, -19.2) * mm});
            skLineSegment(sketch, "E718", {"start": v(4.3, -19.2) * mm, "end": v(3.05, -18.14) * mm});
            skLineSegment(sketch, "E719", {"start": v(3.05, -18.14) * mm, "end": v(1.79, -16.95) * mm});
            skLineSegment(sketch, "E720", {"start": v(1.79, -16.95) * mm, "end": v(2.38, -16.3) * mm});
            skLineSegment(sketch, "E721", {"start": v(2.38, -16.3) * mm, "end": v(2.96, -15.63) * mm});
            skLineSegment(sketch, "E722", {"start": v(2.96, -15.63) * mm, "end": v(3.55, -14.93) * mm});
            skLineSegment(sketch, "E723", {"start": v(3.55, -14.93) * mm, "end": v(4.13, -14.21) * mm});
            skLineSegment(sketch, "E724", {"start": v(4.13, -14.21) * mm, "end": v(4.71, -13.47) * mm});
            skLineSegment(sketch, "E725", {"start": v(4.71, -13.47) * mm, "end": v(5.3, -12.71) * mm});
            skLineSegment(sketch, "E726", {"start": v(5.3, -12.71) * mm, "end": v(5.87, -11.93) * mm});
            skLineSegment(sketch, "E727", {"start": v(5.87, -11.93) * mm, "end": v(6.44, -11.14) * mm});
            skLineSegment(sketch, "E728", {"start": v(6.44, -11.14) * mm, "end": v(7.4, -11.04) * mm});
            skLineSegment(sketch, "E729", {"start": v(7.4, -11.04) * mm, "end": v(8.36, -10.94) * mm});
            skLineSegment(sketch, "E730", {"start": v(8.36, -10.94) * mm, "end": v(9.3, -10.81) * mm});
            skLineSegment(sketch, "E731", {"start": v(9.3, -10.81) * mm, "end": v(10.23, -10.68) * mm});
            skLineSegment(sketch, "E732", {"start": v(10.23, -10.68) * mm, "end": v(11.15, -10.53) * mm});
            skLineSegment(sketch, "E733", {"start": v(11.15, -10.53) * mm, "end": v(12.05, -10.37) * mm});
            skLineSegment(sketch, "E734", {"start": v(12.05, -10.37) * mm, "end": v(12.94, -10.2) * mm});
            skLineSegment(sketch, "E735", {"start": v(12.94, -10.2) * mm, "end": v(13.82, -10.02) * mm});
            skLineSegment(sketch, "E736", {"start": v(13.82, -10.02) * mm, "end": v(13.92, -10.4) * mm});
            skLineSegment(sketch, "E737", {"start": v(13.92, -10.4) * mm, "end": v(14, -10.78) * mm});
            skLineSegment(sketch, "E738", {"start": v(14, -10.78) * mm, "end": v(14.09, -11.16) * mm});
            skLineSegment(sketch, "E739", {"start": v(14.09, -11.16) * mm, "end": v(14.17, -11.53) * mm});
            skLineSegment(sketch, "E740", {"start": v(14.17, -11.53) * mm, "end": v(14.24, -11.9) * mm});
            skLineSegment(sketch, "E741", {"start": v(14.24, -11.9) * mm, "end": v(14.3, -12.26) * mm});
            skLineSegment(sketch, "E742", {"start": v(14.3, -12.26) * mm, "end": v(14.38, -12.62) * mm});
            skLineSegment(sketch, "E743", {"start": v(14.38, -12.62) * mm, "end": v(14.45, -12.97) * mm});
            skLineSegment(sketch, "E744", {"start": v(18.47, -6) * mm, "end": v(18.13, -6.12) * mm});
            skLineSegment(sketch, "E745", {"start": v(18.13, -6.12) * mm, "end": v(17.78, -6.25) * mm});
            skLineSegment(sketch, "E746", {"start": v(17.78, -6.25) * mm, "end": v(17.43, -6.38) * mm});
            skLineSegment(sketch, "E747", {"start": v(17.43, -6.38) * mm, "end": v(17.07, -6.5) * mm});
            skLineSegment(sketch, "E748", {"start": v(17.07, -6.5) * mm, "end": v(16.71, -6.61) * mm});
            skLineSegment(sketch, "E749", {"start": v(16.71, -6.61) * mm, "end": v(16.34, -6.72) * mm});
            skLineSegment(sketch, "E750", {"start": v(16.34, -6.72) * mm, "end": v(15.98, -6.83) * mm});
            skLineSegment(sketch, "E751", {"start": v(15.98, -6.83) * mm, "end": v(15.6, -6.93) * mm});
            skLineSegment(sketch, "E752", {"start": v(15.6, -6.93) * mm, "end": v(15.33, -6.09) * mm});
            skLineSegment(sketch, "E753", {"start": v(15.33, -6.09) * mm, "end": v(15.04, -5.23) * mm});
            skLineSegment(sketch, "E754", {"start": v(15.04, -5.23) * mm, "end": v(14.73, -4.37) * mm});
            skLineSegment(sketch, "E755", {"start": v(14.73, -4.37) * mm, "end": v(14.4, -3.5) * mm});
            skLineSegment(sketch, "E756", {"start": v(14.4, -3.5) * mm, "end": v(14.06, -2.61) * mm});
            skLineSegment(sketch, "E757", {"start": v(14.06, -2.61) * mm, "end": v(13.7, -1.73) * mm});
            skLineSegment(sketch, "E758", {"start": v(13.7, -1.73) * mm, "end": v(13.32, -0.84) * mm});
            skLineSegment(sketch, "E759", {"start": v(13.32, -0.84) * mm, "end": v(12.92, 0.04) * mm});
            skLineSegment(sketch, "E760", {"start": v(12.92, 0.04) * mm, "end": v(13.32, 0.93) * mm});
            skLineSegment(sketch, "E761", {"start": v(13.32, 0.93) * mm, "end": v(13.7, 1.81) * mm});
            skLineSegment(sketch, "E762", {"start": v(13.7, 1.81) * mm, "end": v(14.07, 2.7) * mm});
            skLineSegment(sketch, "E763", {"start": v(14.07, 2.7) * mm, "end": v(14.42, 3.56) * mm});
            skLineSegment(sketch, "E764", {"start": v(14.42, 3.56) * mm, "end": v(14.75, 4.43) * mm});
            skLineSegment(sketch, "E765", {"start": v(14.75, 4.43) * mm, "end": v(15.06, 5.28) * mm});
            skLineSegment(sketch, "E766", {"start": v(15.06, 5.28) * mm, "end": v(15.34, 6.13) * mm});
            skLineSegment(sketch, "E767", {"start": v(15.34, 6.13) * mm, "end": v(15.6, 6.98) * mm});
            skLineSegment(sketch, "E768", {"start": v(15.6, 6.98) * mm, "end": v(17.8, 6.27) * mm});
            skLineSegment(sketch, "E769", {"start": v(17.8, 6.27) * mm, "end": v(19.76, 5.48) * mm});
            skLineSegment(sketch, "E770", {"start": v(19.76, 5.48) * mm, "end": v(21.45, 4.64) * mm});
            skLineSegment(sketch, "E771", {"start": v(21.45, 4.64) * mm, "end": v(22.86, 3.76) * mm});
            skLineSegment(sketch, "E772", {"start": v(22.86, 3.76) * mm, "end": v(24, 2.84) * mm});
            skLineSegment(sketch, "E773", {"start": v(24, 2.84) * mm, "end": v(24.82, 1.9) * mm});
            skLineSegment(sketch, "E774", {"start": v(24.82, 1.9) * mm, "end": v(25.32, 0.95) * mm});
            skLineSegment(sketch, "E775", {"start": v(25.32, 0.95) * mm, "end": v(25.5, 0) * mm});
            skLineSegment(sketch, "E776", {"start": v(25.5, 0) * mm, "end": v(25.37, -0.8) * mm});
            skLineSegment(sketch, "E777", {"start": v(25.37, -0.8) * mm, "end": v(25.02, -1.6) * mm});
            skLineSegment(sketch, "E778", {"start": v(25.02, -1.6) * mm, "end": v(24.44, -2.38) * mm});
            skLineSegment(sketch, "E779", {"start": v(24.44, -2.38) * mm, "end": v(23.64, -3.16) * mm});
            skLineSegment(sketch, "E780", {"start": v(23.64, -3.16) * mm, "end": v(22.64, -3.92) * mm});
            skLineSegment(sketch, "E781", {"start": v(22.64, -3.92) * mm, "end": v(21.44, -4.65) * mm});
            skLineSegment(sketch, "E782", {"start": v(21.44, -4.65) * mm, "end": v(20.04, -5.35) * mm});
            skLineSegment(sketch, "E783", {"start": v(20.04, -5.35) * mm, "end": v(18.47, -6) * mm});
            skLineSegment(sketch, "E784", {"start": v(0, -18.78) * mm, "end": v(0, -25) * mm});
            skLineSegment(sketch, "E785", {"start": v(-11.14, -25) * mm, "end": v(11.14, -25) * mm});
            skSolve(sketch);
        }
        {
            var Q0;
            Q0=makeQuery(id+"F0.imprint","IMPRINT",FACE,{"disambiguationData":[TD([[makeQuery(id+"F0.imprint","IMPRINT",EDGE,{"derivedFrom":sQuery(id+"F0.wireOp",EDGE,"E0")}),1.0]])]});
            var Q1;
            Q1=makeQuery(id+"F0.imprint","IMPRINT",FACE,{"disambiguationData":[TD([[makeQuery(id+"F0.imprint","IMPRINT",EDGE,{"derivedFrom":sQuery(id+"F0.wireOp",EDGE,"E32")}),1.0]])]});
            var Q2;
            Q2=makeQuery(id+"F0.imprint","IMPRINT",FACE,{"disambiguationData":[TD([[makeQuery(id+"F0.imprint","IMPRINT",EDGE,{"derivedFrom":sQuery(id+"F0.wireOp",EDGE,"E0")}),-1.0]])]});
            var Q3;
            Q3=makeQuery(id+"F0.imprint","IMPRINT",FACE,{"disambiguationData":[TD([[makeQuery(id+"F0.imprint","IMPRINT",EDGE,{"derivedFrom":sQuery(id+"F0.wireOp",EDGE,"E224")}),-1.0]])]});
            var Q4;
            Q4=makeQuery(id+"F0.imprint","IMPRINT",FACE,{"disambiguationData":[TD([[makeQuery(id+"F0.imprint","IMPRINT",EDGE,{"derivedFrom":sQuery(id+"F0.wireOp",EDGE,"E560")}),-1.0]])]});
            var Q5;
            Q5=makeQuery(id+"F0.imprint","IMPRINT",FACE,{"disambiguationData":[TD([[makeQuery(id+"F0.imprint","IMPRINT",EDGE,{"derivedFrom":sQuery(id+"F0.wireOp",EDGE,"E608")}),-1.0]])]});
            var Q6;
            Q6=makeQuery(id+"F0.imprint","IMPRINT",FACE,{"disambiguationData":[TD([[makeQuery(id+"F0.imprint","IMPRINT",EDGE,{"derivedFrom":sQuery(id+"F0.wireOp",EDGE,"E648")}),-1.0]])]});
            var Q7;
            Q7=makeQuery(id+"F0.imprint","IMPRINT",FACE,{"disambiguationData":[TD([[makeQuery(id+"F0.imprint","IMPRINT",EDGE,{"derivedFrom":sQuery(id+"F0.wireOp",EDGE,"E696")}),-1.0]])]});
            var Q8;
            Q8=makeQuery(id+"F0.imprint","IMPRINT",FACE,{"disambiguationData":[TD([[makeQuery(id+"F0.imprint","IMPRINT",EDGE,{"derivedFrom":sQuery(id+"F0.wireOp",EDGE,"E744")}),-1.0]])]});
            var Q9;
            Q9=makeQuery(id+"F0.imprint","IMPRINT",FACE,{"disambiguationData":[TD([[makeQuery(id+"F0.imprint","IMPRINT",EDGE,{"derivedFrom":sQuery(id+"F0.wireOp",EDGE,"E368")}),-1.0]])]});
            var Q10;
            Q10=makeQuery(id+"F0.imprint","IMPRINT",FACE,{"disambiguationData":[TD([[makeQuery(id+"F0.imprint","IMPRINT",EDGE,{"derivedFrom":sQuery(id+"F0.wireOp",EDGE,"E432")}),-1.0]])]});
            var Q11;
            Q11=makeQuery(id+"F0.imprint","IMPRINT",FACE,{"disambiguationData":[TD([[makeQuery(id+"F0.imprint","IMPRINT",EDGE,{"derivedFrom":sQuery(id+"F0.wireOp",EDGE,"E464")}),-1.0]])]});
            var Q12;
            Q12=makeQuery(id+"F0.imprint","IMPRINT",FACE,{"disambiguationData":[TD([[makeQuery(id+"F0.imprint","IMPRINT",EDGE,{"derivedFrom":sQuery(id+"F0.wireOp",EDGE,"E528")}),-1.0]])]});
            var Q13;
            Q13=makeQuery(id+"F0.imprint","IMPRINT",FACE,{"disambiguationData":[TD([[makeQuery(id+"F0.imprint","IMPRINT",EDGE,{"derivedFrom":sQuery(id+"F0.wireOp",EDGE,"E400")}),-1.0]])]});
            var Q14;
            Q14=makeQuery(id+"F0.imprint","IMPRINT",FACE,{"disambiguationData":[TD([[makeQuery(id+"F0.imprint","IMPRINT",EDGE,{"derivedFrom":sQuery(id+"F0.wireOp",EDGE,"E496")}),-1.0]])]});
            extrude(context, id + "F1", {"entities" : qUnion([Q0, Q1, Q2, Q3, Q4, Q5, Q6, Q7, Q8, Q9, Q10, Q11, Q12, Q13, Q14]), "oppositeDirection" : true, "depth" : 2 * mm});
        }
        {
            var Q0;
            Q0=makeQuery(id+"F0.imprint","IMPRINT",FACE,{"disambiguationData":[TD([[makeQuery(id+"F0.imprint","IMPRINT",EDGE,{"derivedFrom":sQuery(id+"F0.wireOp",EDGE,"E32")}),1.0]])]});
            var Q1;
            Q1=makeQuery(id+"F0.imprint","IMPRINT",FACE,{"disambiguationData":[TD([[makeQuery(id+"F0.imprint","IMPRINT",EDGE,{"derivedFrom":sQuery(id+"F0.wireOp",EDGE,"E0")}),-1.0]])]});
            extrude(context, id + "F2", {"entities" : qUnion([Q0, Q1]), "operationType" : NewBodyOperationType.ADD, "depth" : 3 * mm});
        }
        {
            var Q0;
            Q0=sQuery(id+"F0.wireOp",EDGE,"E785");
            var Q1;
            Q1=sQuery(id+"F0.wireOp",VERTEX,"E785.end");
            cPlane(context, id + "F3", {"entities" : qUnion([Q0, Q1]), "cplaneType" : CPlaneType.LINE_POINT, "offset" : 25 * mm, "width" : 150 * mm, "height" : 150 * mm});
        }
        {
            var Q0;
            Q0=qCreatedBy(id+"F3.planeOp",FACE);
            var sketch = newSketch(context, id + "F4", { "sketchPlane" : qUnion([Q0])});
            skLineSegment(sketch, "E786", {"start": v(-25, -2) * mm, "end": v(-25, 3) * mm});
            skLineSegment(sketch, "E787", {"start": v(-25, 3) * mm, "end": v(-32.5, 5.5) * mm});
            skLineSegment(sketch, "E788", {"start": v(-32.5, 5.5) * mm, "end": v(-32.5, 8) * mm});
            skLineSegment(sketch, "E789", {"start": v(-32.5, 8) * mm, "end": v(-35, 8) * mm});
            skLineSegment(sketch, "E790", {"start": v(-35, 8) * mm, "end": v(-35, -7) * mm});
            skLineSegment(sketch, "E791", {"start": v(-35, -7) * mm, "end": v(-32.5, -7) * mm});
            skLineSegment(sketch, "E792", {"start": v(-32.5, -7) * mm, "end": v(-32.5, -4.5) * mm});
            skLineSegment(sketch, "E793", {"start": v(-32.5, -4.5) * mm, "end": v(-25, -2) * mm});
            skLineSegment(sketch, "E794", {"start": v(-25, 0.5) * mm, "end": v(-35, 0.5) * mm});
            skPoint(sketch, "E794.endSnap0", {"position": v(-35, 0.5) * mm});
            skLineSegment(sketch, "E795.bottom", {"start": v(-25, -2) * mm, "end": v(-24, -2) * mm});
            skLineSegment(sketch, "E795.top", {"start": v(-25, 3) * mm, "end": v(-24, 3) * mm});
            skLineSegment(sketch, "E795.right", {"start": v(-24, -2) * mm, "end": v(-24, 3) * mm});
            skSolve(sketch);
        }
        {
            var Q0;
            {var subQ3=sQuery(id+"F4.wireOp",EDGE,"E787");Q0=makeQuery(id+"F4.imprint","IMPRINT",FACE,{"disambiguationData":[TD([[makeQuery(id+"F4.imprint","IMPRINT",EDGE,{"derivedFrom":subQ3}),1.0]])]});}
            var Q1;
            {var subQ1=sQuery(id+"F4.wireOp",EDGE,"E791");Q1=makeQuery(id+"F4.imprint","IMPRINT",FACE,{"disambiguationData":[TD([[makeQuery(id+"F4.imprint","IMPRINT",EDGE,{"derivedFrom":subQ1}),1.0]])]});}
            var Q2;
            {var subQ3=sQuery(id+"F4.wireOp",EDGE,"E795.bottom");Q2=makeQuery(id+"F4.imprint","IMPRINT",FACE,{"disambiguationData":[TD([[makeQuery(id+"F4.imprint","IMPRINT",EDGE,{"derivedFrom":subQ3}),1.0]])]});}
            extrude(context, id + "F5", {"entities" : qUnion([Q0, Q1, Q2]), "operationType" : NewBodyOperationType.ADD, "oppositeDirection" : true, "depth" : 24 * mm, "hasSecondDirection" : true, "secondDirectionOppositeDirection" : false, "secondDirectionDepth" : 2 * mm});
        }
    });
